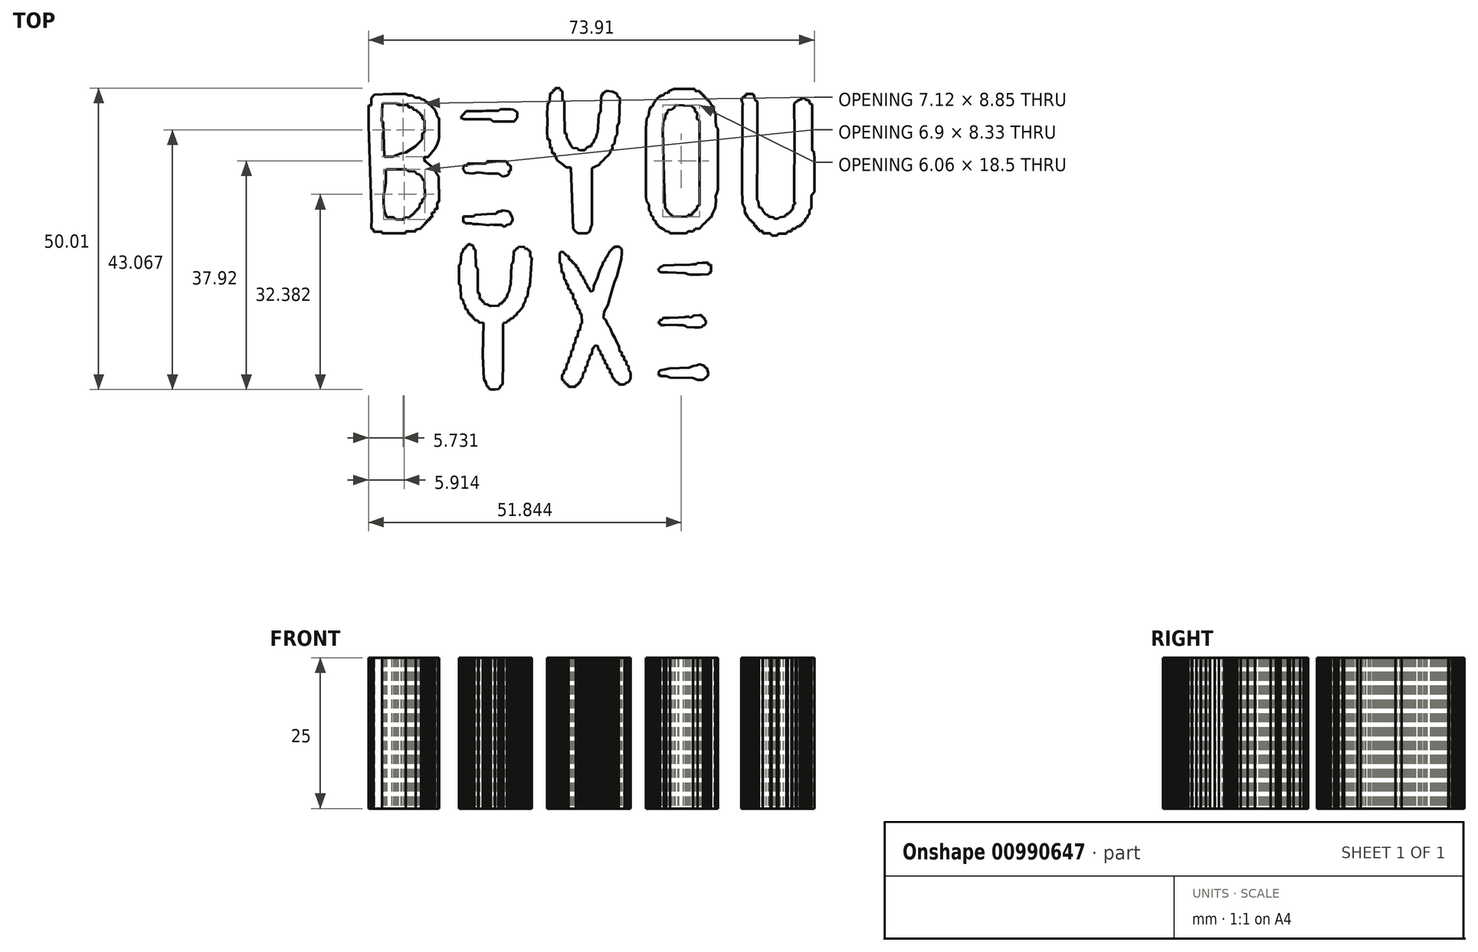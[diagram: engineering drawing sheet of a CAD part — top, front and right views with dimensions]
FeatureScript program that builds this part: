
annotation { "Feature Type Name" : "Feature", "Feature Type Description" : "" }
export const myFeature = defineFeature(function(context is Context, id is Id, definition is map)
    precondition{}
    {
        {
            var Q0;
            Q0=qCreatedBy(makeId("Top.planeOp"), FACE);
            var sketch = newSketch(context, id + "F0", { "sketchPlane" : qUnion([Q0])});
            skLineSegment(sketch, "E0", {"start": v(-34.3, -5.43) * mm, "end": v(-34.81, 9.8) * mm});
            skLineSegment(sketch, "E1", {"start": v(-34.81, 9.8) * mm, "end": v(-34.81, 13.18) * mm});
            skLineSegment(sketch, "E2", {"start": v(-34.81, 13.18) * mm, "end": v(-34.36, 13.18) * mm});
            skLineSegment(sketch, "E3", {"start": v(-34.36, 13.18) * mm, "end": v(-34.36, 14.36) * mm});
            skLineSegment(sketch, "E4", {"start": v(-34.36, 14.36) * mm, "end": v(-33.86, 14.98) * mm});
            skLineSegment(sketch, "E5", {"start": v(-33.86, 14.98) * mm, "end": v(-31, 15.08) * mm});
            skLineSegment(sketch, "E6", {"start": v(-31, 15.08) * mm, "end": v(-30.33, 15.08) * mm});
            skLineSegment(sketch, "E7", {"start": v(-30.33, 15.08) * mm, "end": v(-29.68, 15.08) * mm});
            skLineSegment(sketch, "E8", {"start": v(-29.68, 15.08) * mm, "end": v(-28.68, 15.08) * mm});
            skLineSegment(sketch, "E9", {"start": v(-28.68, 15.08) * mm, "end": v(-28.46, 14.98) * mm});
            skLineSegment(sketch, "E10", {"start": v(-28.46, 14.98) * mm, "end": v(-28.18, 14.86) * mm});
            skLineSegment(sketch, "E11", {"start": v(-28.18, 14.86) * mm, "end": v(-27.9, 14.86) * mm});
            skLineSegment(sketch, "E12", {"start": v(-27.9, 14.86) * mm, "end": v(-27.49, 14.86) * mm});
            skLineSegment(sketch, "E13", {"start": v(-27.49, 14.86) * mm, "end": v(-27.28, 14.62) * mm});
            skLineSegment(sketch, "E14", {"start": v(-27.28, 14.62) * mm, "end": v(-27.05, 14.47) * mm});
            skLineSegment(sketch, "E15", {"start": v(-27.05, 14.47) * mm, "end": v(-26.25, 14.47) * mm});
            skLineSegment(sketch, "E16", {"start": v(-26.25, 14.47) * mm, "end": v(-26.04, 14.22) * mm});
            skLineSegment(sketch, "E17", {"start": v(-26.04, 14.22) * mm, "end": v(-25.7, 14.11) * mm});
            skLineSegment(sketch, "E18", {"start": v(-25.7, 14.11) * mm, "end": v(-25.38, 14) * mm});
            skLineSegment(sketch, "E19", {"start": v(-25.38, 14) * mm, "end": v(-25.38, 13.8) * mm});
            skLineSegment(sketch, "E20", {"start": v(-25.38, 13.8) * mm, "end": v(-24.94, 13.68) * mm});
            skLineSegment(sketch, "E21", {"start": v(-24.94, 13.68) * mm, "end": v(-24.94, 13.52) * mm});
            skLineSegment(sketch, "E22", {"start": v(-24.94, 13.52) * mm, "end": v(-24.86, 13.42) * mm});
            skLineSegment(sketch, "E23", {"start": v(-24.86, 13.42) * mm, "end": v(-24.67, 13.33) * mm});
            skLineSegment(sketch, "E24", {"start": v(-24.67, 13.33) * mm, "end": v(-24.4, 13.23) * mm});
            skLineSegment(sketch, "E25", {"start": v(-24.4, 13.23) * mm, "end": v(-24.3, 12.92) * mm});
            skLineSegment(sketch, "E26", {"start": v(-24.3, 12.92) * mm, "end": v(-24.1, 12.8) * mm});
            skLineSegment(sketch, "E27", {"start": v(-24.1, 12.8) * mm, "end": v(-23.97, 12.65) * mm});
            skLineSegment(sketch, "E28", {"start": v(-23.97, 12.65) * mm, "end": v(-23.87, 12.54) * mm});
            skLineSegment(sketch, "E29", {"start": v(-23.87, 12.54) * mm, "end": v(-23.67, 12.15) * mm});
            skLineSegment(sketch, "E30", {"start": v(-23.67, 12.15) * mm, "end": v(-23.47, 11.72) * mm});
            skLineSegment(sketch, "E31", {"start": v(-23.47, 11.72) * mm, "end": v(-23.48, 11.48) * mm});
            skLineSegment(sketch, "E32", {"start": v(-23.48, 11.48) * mm, "end": v(-23.32, 11.22) * mm});
            skLineSegment(sketch, "E33", {"start": v(-23.32, 11.22) * mm, "end": v(-23.2, 11.12) * mm});
            skLineSegment(sketch, "E34", {"start": v(-23.2, 11.12) * mm, "end": v(-23.12, 10.84) * mm});
            skLineSegment(sketch, "E35", {"start": v(-23.12, 10.84) * mm, "end": v(-23.12, 7.9) * mm});
            skLineSegment(sketch, "E36", {"start": v(-23.12, 7.9) * mm, "end": v(-23.2, 7.48) * mm});
            skLineSegment(sketch, "E37", {"start": v(-23.2, 7.48) * mm, "end": v(-23.46, 6.68) * mm});
            skLineSegment(sketch, "E38", {"start": v(-23.46, 6.68) * mm, "end": v(-23.84, 5.97) * mm});
            skLineSegment(sketch, "E39", {"start": v(-23.84, 5.97) * mm, "end": v(-24.26, 5.45) * mm});
            skLineSegment(sketch, "E40", {"start": v(-24.26, 5.45) * mm, "end": v(-24.54, 5.11) * mm});
            skLineSegment(sketch, "E41", {"start": v(-24.54, 5.11) * mm, "end": v(-24.94, 4.62) * mm});
            skLineSegment(sketch, "E42", {"start": v(-24.94, 4.62) * mm, "end": v(-25.58, 4.62) * mm});
            skLineSegment(sketch, "E43", {"start": v(-25.58, 4.62) * mm, "end": v(-25.58, 4.23) * mm});
            skLineSegment(sketch, "E44", {"start": v(-25.58, 4.23) * mm, "end": v(-25.38, 3.9) * mm});
            skLineSegment(sketch, "E45", {"start": v(-25.38, 3.9) * mm, "end": v(-24.94, 3.54) * mm});
            skLineSegment(sketch, "E46", {"start": v(-24.94, 3.54) * mm, "end": v(-24.55, 3.21) * mm});
            skLineSegment(sketch, "E47", {"start": v(-24.55, 3.21) * mm, "end": v(-24.02, 2.79) * mm});
            skLineSegment(sketch, "E48", {"start": v(-24.02, 2.79) * mm, "end": v(-23.66, 2.15) * mm});
            skLineSegment(sketch, "E49", {"start": v(-23.66, 2.15) * mm, "end": v(-23.2, 1.35) * mm});
            skLineSegment(sketch, "E50", {"start": v(-23.2, 1.35) * mm, "end": v(-23.12, -2.78) * mm});
            skLineSegment(sketch, "E51", {"start": v(-23.12, -2.78) * mm, "end": v(-23.46, -2.97) * mm});
            skLineSegment(sketch, "E52", {"start": v(-23.46, -2.97) * mm, "end": v(-23.44, -3.7) * mm});
            skLineSegment(sketch, "E53", {"start": v(-23.44, -3.7) * mm, "end": v(-23.29, -3.98) * mm});
            skLineSegment(sketch, "E54", {"start": v(-23.29, -3.98) * mm, "end": v(-23.81, -3.98) * mm});
            skLineSegment(sketch, "E55", {"start": v(-23.81, -3.98) * mm, "end": v(-23.88, -4.63) * mm});
            skLineSegment(sketch, "E56", {"start": v(-23.88, -4.63) * mm, "end": v(-24.29, -4.64) * mm});
            skLineSegment(sketch, "E57", {"start": v(-24.29, -4.64) * mm, "end": v(-24.28, -5.37) * mm});
            skLineSegment(sketch, "E58", {"start": v(-24.28, -5.37) * mm, "end": v(-24.64, -5.37) * mm});
            skLineSegment(sketch, "E59", {"start": v(-24.64, -5.37) * mm, "end": v(-24.64, -5.8) * mm});
            skLineSegment(sketch, "E60", {"start": v(-24.64, -5.8) * mm, "end": v(-25.06, -5.8) * mm});
            skLineSegment(sketch, "E61", {"start": v(-25.06, -5.8) * mm, "end": v(-25.06, -6.16) * mm});
            skLineSegment(sketch, "E62", {"start": v(-25.06, -6.16) * mm, "end": v(-25.38, -6.16) * mm});
            skLineSegment(sketch, "E63", {"start": v(-25.38, -6.16) * mm, "end": v(-25.37, -6.52) * mm});
            skLineSegment(sketch, "E64", {"start": v(-25.37, -6.52) * mm, "end": v(-25.62, -6.67) * mm});
            skLineSegment(sketch, "E65", {"start": v(-25.62, -6.67) * mm, "end": v(-25.8, -6.9) * mm});
            skLineSegment(sketch, "E66", {"start": v(-25.8, -6.9) * mm, "end": v(-26.12, -7.07) * mm});
            skLineSegment(sketch, "E67", {"start": v(-26.12, -7.07) * mm, "end": v(-26.12, -7.3) * mm});
            skLineSegment(sketch, "E68", {"start": v(-26.12, -7.3) * mm, "end": v(-26.98, -7.38) * mm});
            skLineSegment(sketch, "E69", {"start": v(-26.98, -7.38) * mm, "end": v(-26.95, -7.7) * mm});
            skLineSegment(sketch, "E70", {"start": v(-26.95, -7.7) * mm, "end": v(-28.6, -7.7) * mm});
            skLineSegment(sketch, "E71", {"start": v(-28.6, -7.7) * mm, "end": v(-28.64, -8.06) * mm});
            skLineSegment(sketch, "E72", {"start": v(-28.64, -8.06) * mm, "end": v(-32.55, -8.06) * mm});
            skLineSegment(sketch, "E73", {"start": v(-32.55, -8.06) * mm, "end": v(-32.56, -7.78) * mm});
            skLineSegment(sketch, "E74", {"start": v(-32.56, -7.78) * mm, "end": v(-33.96, -7.78) * mm});
            skLineSegment(sketch, "E75", {"start": v(-33.96, -7.78) * mm, "end": v(-33.97, -7.37) * mm});
            skLineSegment(sketch, "E76", {"start": v(-33.97, -7.37) * mm, "end": v(-34.36, -7.3) * mm});
            skLineSegment(sketch, "E77", {"start": v(-34.36, -7.3) * mm, "end": v(-34.3, -5.43) * mm});
            skLineSegment(sketch, "E78", {"start": v(-19.52, 11.12) * mm, "end": v(-19.02, 11.74) * mm});
            skLineSegment(sketch, "E79", {"start": v(-19.02, 11.74) * mm, "end": v(-18.6, 12.25) * mm});
            skLineSegment(sketch, "E80", {"start": v(-18.6, 12.25) * mm, "end": v(-17.58, 12.25) * mm});
            skLineSegment(sketch, "E81", {"start": v(-17.58, 12.25) * mm, "end": v(-15.95, 12.25) * mm});
            skLineSegment(sketch, "E82", {"start": v(-15.95, 12.25) * mm, "end": v(-15.27, 12.26) * mm});
            skLineSegment(sketch, "E83", {"start": v(-15.27, 12.26) * mm, "end": v(-13.29, 12.3) * mm});
            skLineSegment(sketch, "E84", {"start": v(-13.29, 12.3) * mm, "end": v(-12.97, 12.54) * mm});
            skLineSegment(sketch, "E85", {"start": v(-12.97, 12.54) * mm, "end": v(-12.51, 12.54) * mm});
            skLineSegment(sketch, "E86", {"start": v(-12.51, 12.54) * mm, "end": v(-12.05, 12.54) * mm});
            skLineSegment(sketch, "E87", {"start": v(-12.05, 12.54) * mm, "end": v(-11.24, 12.54) * mm});
            skLineSegment(sketch, "E88", {"start": v(-11.24, 12.54) * mm, "end": v(-10.76, 12.5) * mm});
            skLineSegment(sketch, "E89", {"start": v(-10.76, 12.5) * mm, "end": v(-10.18, 12.02) * mm});
            skLineSegment(sketch, "E90", {"start": v(-10.18, 12.02) * mm, "end": v(-10.16, 11.12) * mm});
            skLineSegment(sketch, "E91", {"start": v(-10.16, 11.12) * mm, "end": v(-10.66, 10.52) * mm});
            skLineSegment(sketch, "E92", {"start": v(-10.66, 10.52) * mm, "end": v(-11.52, 10.52) * mm});
            skLineSegment(sketch, "E93", {"start": v(-11.52, 10.52) * mm, "end": v(-14.14, 10.52) * mm});
            skLineSegment(sketch, "E94", {"start": v(-14.14, 10.52) * mm, "end": v(-14.57, 10.87) * mm});
            skLineSegment(sketch, "E95", {"start": v(-14.57, 10.87) * mm, "end": v(-15.38, 10.87) * mm});
            skLineSegment(sketch, "E96", {"start": v(-15.38, 10.87) * mm, "end": v(-18.96, 10.87) * mm});
            skLineSegment(sketch, "E97", {"start": v(-18.96, 10.87) * mm, "end": v(-19.52, 11.12) * mm});
            skLineSegment(sketch, "E98", {"start": v(-19.13, 2.59) * mm, "end": v(-19.08, 3.18) * mm});
            skLineSegment(sketch, "E99", {"start": v(-19.08, 3.18) * mm, "end": v(-18.7, 3.18) * mm});
            skLineSegment(sketch, "E100", {"start": v(-18.7, 3.18) * mm, "end": v(-18.43, 3.18) * mm});
            skLineSegment(sketch, "E101", {"start": v(-18.43, 3.18) * mm, "end": v(-18.43, 3.54) * mm});
            skLineSegment(sketch, "E102", {"start": v(-18.43, 3.54) * mm, "end": v(-16.83, 3.54) * mm});
            skLineSegment(sketch, "E103", {"start": v(-16.83, 3.54) * mm, "end": v(-15.38, 3.54) * mm});
            skLineSegment(sketch, "E104", {"start": v(-15.38, 3.54) * mm, "end": v(-15.01, 4) * mm});
            skLineSegment(sketch, "E105", {"start": v(-15.01, 4) * mm, "end": v(-14.15, 3.9) * mm});
            skLineSegment(sketch, "E106", {"start": v(-14.15, 3.9) * mm, "end": v(-13.26, 3.9) * mm});
            skLineSegment(sketch, "E107", {"start": v(-13.26, 3.9) * mm, "end": v(-12.37, 3.9) * mm});
            skLineSegment(sketch, "E108", {"start": v(-12.37, 3.9) * mm, "end": v(-11.95, 3.9) * mm});
            skLineSegment(sketch, "E109", {"start": v(-11.95, 3.9) * mm, "end": v(-11.53, 3.18) * mm});
            skLineSegment(sketch, "E110", {"start": v(-11.53, 3.18) * mm, "end": v(-11.24, 3.18) * mm});
            skLineSegment(sketch, "E111", {"start": v(-11.24, 3.18) * mm, "end": v(-11.22, 2.3) * mm});
            skLineSegment(sketch, "E112", {"start": v(-11.22, 2.3) * mm, "end": v(-11.52, 2.3) * mm});
            skLineSegment(sketch, "E113", {"start": v(-11.52, 2.3) * mm, "end": v(-11.51, 1.88) * mm});
            skLineSegment(sketch, "E114", {"start": v(-11.51, 1.88) * mm, "end": v(-11.8, 1.53) * mm});
            skLineSegment(sketch, "E115", {"start": v(-11.8, 1.53) * mm, "end": v(-12.58, 1.35) * mm});
            skLineSegment(sketch, "E116", {"start": v(-12.58, 1.35) * mm, "end": v(-13.23, 1.88) * mm});
            skLineSegment(sketch, "E117", {"start": v(-13.23, 1.88) * mm, "end": v(-14.57, 1.88) * mm});
            skLineSegment(sketch, "E118", {"start": v(-14.57, 1.88) * mm, "end": v(-15.1, 1.88) * mm});
            skLineSegment(sketch, "E119", {"start": v(-15.1, 1.88) * mm, "end": v(-15.83, 1.96) * mm});
            skLineSegment(sketch, "E120", {"start": v(-15.83, 1.96) * mm, "end": v(-16.64, 2.04) * mm});
            skLineSegment(sketch, "E121", {"start": v(-16.64, 2.04) * mm, "end": v(-17.58, 1.88) * mm});
            skLineSegment(sketch, "E122", {"start": v(-17.58, 1.88) * mm, "end": v(-18.7, 2) * mm});
            skLineSegment(sketch, "E123", {"start": v(-18.7, 2) * mm, "end": v(-19.13, 2.59) * mm});
            skLineSegment(sketch, "E124", {"start": v(-18.8, -6.4) * mm, "end": v(-18.8, -6.17) * mm});
            skLineSegment(sketch, "E125", {"start": v(-18.8, -6.17) * mm, "end": v(-19.13, -6.17) * mm});
            skLineSegment(sketch, "E126", {"start": v(-19.13, -6.17) * mm, "end": v(-19.14, -5.83) * mm});
            skLineSegment(sketch, "E127", {"start": v(-19.14, -5.83) * mm, "end": v(-19.13, -5.77) * mm});
            skLineSegment(sketch, "E128", {"start": v(-19.13, -5.77) * mm, "end": v(-19.14, -5.64) * mm});
            skLineSegment(sketch, "E129", {"start": v(-19.14, -5.64) * mm, "end": v(-19.1, -5.27) * mm});
            skLineSegment(sketch, "E130", {"start": v(-19.1, -5.27) * mm, "end": v(-18.4, -5.27) * mm});
            skLineSegment(sketch, "E131", {"start": v(-18.4, -5.27) * mm, "end": v(-17.37, -5.27) * mm});
            skLineSegment(sketch, "E132", {"start": v(-17.37, -5.27) * mm, "end": v(-17.13, -4.97) * mm});
            skLineSegment(sketch, "E133", {"start": v(-17.13, -4.97) * mm, "end": v(-14.14, -4.8) * mm});
            skLineSegment(sketch, "E134", {"start": v(-14.14, -4.8) * mm, "end": v(-13.74, -4.85) * mm});
            skLineSegment(sketch, "E135", {"start": v(-13.74, -4.85) * mm, "end": v(-13.53, -4.6) * mm});
            skLineSegment(sketch, "E136", {"start": v(-13.53, -4.6) * mm, "end": v(-13.19, -4.4) * mm});
            skLineSegment(sketch, "E137", {"start": v(-13.19, -4.4) * mm, "end": v(-12.9, -4.4) * mm});
            skLineSegment(sketch, "E138", {"start": v(-12.9, -4.4) * mm, "end": v(-12.58, -4.22) * mm});
            skLineSegment(sketch, "E139", {"start": v(-12.58, -4.22) * mm, "end": v(-11.84, -4.35) * mm});
            skLineSegment(sketch, "E140", {"start": v(-11.84, -4.35) * mm, "end": v(-11.51, -4.45) * mm});
            skLineSegment(sketch, "E141", {"start": v(-11.51, -4.45) * mm, "end": v(-10.98, -5.38) * mm});
            skLineSegment(sketch, "E142", {"start": v(-10.98, -5.38) * mm, "end": v(-10.9, -5.78) * mm});
            skLineSegment(sketch, "E143", {"start": v(-10.9, -5.78) * mm, "end": v(-11.05, -6.12) * mm});
            skLineSegment(sketch, "E144", {"start": v(-11.05, -6.12) * mm, "end": v(-11.3, -6.5) * mm});
            skLineSegment(sketch, "E145", {"start": v(-11.3, -6.5) * mm, "end": v(-11.9, -6.63) * mm});
            skLineSegment(sketch, "E146", {"start": v(-11.9, -6.63) * mm, "end": v(-12.11, -6.9) * mm});
            skLineSegment(sketch, "E147", {"start": v(-12.11, -6.9) * mm, "end": v(-12.58, -6.9) * mm});
            skLineSegment(sketch, "E148", {"start": v(-12.58, -6.9) * mm, "end": v(-12.65, -6.63) * mm});
            skLineSegment(sketch, "E149", {"start": v(-12.65, -6.63) * mm, "end": v(-14.07, -6.63) * mm});
            skLineSegment(sketch, "E150", {"start": v(-14.07, -6.63) * mm, "end": v(-14.57, -6.58) * mm});
            skLineSegment(sketch, "E151", {"start": v(-14.57, -6.58) * mm, "end": v(-14.78, -6.7) * mm});
            skLineSegment(sketch, "E152", {"start": v(-14.78, -6.7) * mm, "end": v(-15.54, -6.63) * mm});
            skLineSegment(sketch, "E153", {"start": v(-15.54, -6.63) * mm, "end": v(-15.87, -6.6) * mm});
            skLineSegment(sketch, "E154", {"start": v(-15.87, -6.6) * mm, "end": v(-16.53, -6.53) * mm});
            skLineSegment(sketch, "E155", {"start": v(-16.53, -6.53) * mm, "end": v(-17.17, -6.53) * mm});
            skLineSegment(sketch, "E156", {"start": v(-17.17, -6.53) * mm, "end": v(-17.48, -6.5) * mm});
            skLineSegment(sketch, "E157", {"start": v(-17.48, -6.5) * mm, "end": v(-17.78, -6.38) * mm});
            skLineSegment(sketch, "E158", {"start": v(-17.78, -6.38) * mm, "end": v(-18.1, -6.38) * mm});
            skLineSegment(sketch, "E159", {"start": v(-18.1, -6.38) * mm, "end": v(-18.8, -6.4) * mm});
            skLineSegment(sketch, "E160", {"start": v(-3.75, 16.06) * mm, "end": v(-3.92, 15.96) * mm});
            skLineSegment(sketch, "E161", {"start": v(-3.92, 15.96) * mm, "end": v(-3.9, 15.67) * mm});
            skLineSegment(sketch, "E162", {"start": v(-3.9, 15.67) * mm, "end": v(-4.2, 15.67) * mm});
            skLineSegment(sketch, "E163", {"start": v(-4.2, 15.67) * mm, "end": v(-4.3, 15.56) * mm});
            skLineSegment(sketch, "E164", {"start": v(-4.3, 15.56) * mm, "end": v(-4.28, 15.3) * mm});
            skLineSegment(sketch, "E165", {"start": v(-4.28, 15.3) * mm, "end": v(-4.47, 15.2) * mm});
            skLineSegment(sketch, "E166", {"start": v(-4.47, 15.2) * mm, "end": v(-4.68, 15.2) * mm});
            skLineSegment(sketch, "E167", {"start": v(-4.68, 15.2) * mm, "end": v(-4.66, 14.98) * mm});
            skLineSegment(sketch, "E168", {"start": v(-4.66, 14.98) * mm, "end": v(-4.8, 13.6) * mm});
            skLineSegment(sketch, "E169", {"start": v(-4.8, 13.6) * mm, "end": v(-5.05, 13.6) * mm});
            skLineSegment(sketch, "E170", {"start": v(-5.05, 13.6) * mm, "end": v(-5.22, 11.93) * mm});
            skLineSegment(sketch, "E171", {"start": v(-5.22, 11.93) * mm, "end": v(-5.13, 10.54) * mm});
            skPoint(sketch, "E171.endSnap0", {"position": v(-5.13, 12.76) * mm});
            skLineSegment(sketch, "E172", {"start": v(-5.13, 10.54) * mm, "end": v(-5.22, 8.93) * mm});
            skLineSegment(sketch, "E173", {"start": v(-5.22, 8.93) * mm, "end": v(-5.13, 7.52) * mm});
            skLineSegment(sketch, "E174", {"start": v(-5.13, 7.52) * mm, "end": v(-4.79, 7.52) * mm});
            skLineSegment(sketch, "E175", {"start": v(-4.79, 7.52) * mm, "end": v(-4.68, 6.1) * mm});
            skLineSegment(sketch, "E176", {"start": v(-4.68, 6.1) * mm, "end": v(-4.44, 6.23) * mm});
            skLineSegment(sketch, "E177", {"start": v(-4.44, 6.23) * mm, "end": v(-4.38, 5.25) * mm});
            skLineSegment(sketch, "E178", {"start": v(-4.38, 5.25) * mm, "end": v(-3.96, 5.25) * mm});
            skLineSegment(sketch, "E179", {"start": v(-3.96, 5.25) * mm, "end": v(-3.92, 4.62) * mm});
            skLineSegment(sketch, "E180", {"start": v(-3.92, 4.62) * mm, "end": v(-3.56, 4.62) * mm});
            skLineSegment(sketch, "E181", {"start": v(-3.56, 4.62) * mm, "end": v(-3.72, 4.42) * mm});
            skLineSegment(sketch, "E182", {"start": v(-3.72, 4.42) * mm, "end": v(-3.49, 4) * mm});
            skLineSegment(sketch, "E183", {"start": v(-3.49, 4) * mm, "end": v(-2.52, 3.34) * mm});
            skLineSegment(sketch, "E184", {"start": v(-2.52, 3.34) * mm, "end": v(-2, 2.91) * mm});
            skLineSegment(sketch, "E185", {"start": v(-2, 2.91) * mm, "end": v(-1.24, 2.91) * mm});
            skLineSegment(sketch, "E186", {"start": v(-1.24, 2.91) * mm, "end": v(-0.86, -7.3) * mm});
            skLineSegment(sketch, "E187", {"start": v(-0.86, -7.3) * mm, "end": v(-0.47, -7.7) * mm});
            skLineSegment(sketch, "E188", {"start": v(-0.47, -7.7) * mm, "end": v(-0.13, -8.06) * mm});
            skLineSegment(sketch, "E189", {"start": v(-0.13, -8.06) * mm, "end": v(1.46, -8.06) * mm});
            skLineSegment(sketch, "E190", {"start": v(1.46, -8.06) * mm, "end": v(1.86, -7.7) * mm});
            skLineSegment(sketch, "E191", {"start": v(1.86, -7.7) * mm, "end": v(2.1, -6.9) * mm});
            skLineSegment(sketch, "E192", {"start": v(2.1, -6.9) * mm, "end": v(2.22, -6.66) * mm});
            skLineSegment(sketch, "E193", {"start": v(2.22, -6.66) * mm, "end": v(2.26, 2.78) * mm});
            skLineSegment(sketch, "E194", {"start": v(2.26, 2.78) * mm, "end": v(2.62, 2.98) * mm});
            skLineSegment(sketch, "E195", {"start": v(2.62, 2.98) * mm, "end": v(3.42, 3.35) * mm});
            skLineSegment(sketch, "E196", {"start": v(3.42, 3.35) * mm, "end": v(3.71, 3.7) * mm});
            skLineSegment(sketch, "E197", {"start": v(3.71, 3.7) * mm, "end": v(4.14, 4.12) * mm});
            skLineSegment(sketch, "E198", {"start": v(4.14, 4.12) * mm, "end": v(4.45, 4.5) * mm});
            skLineSegment(sketch, "E199", {"start": v(4.45, 4.5) * mm, "end": v(4.88, 4.85) * mm});
            skLineSegment(sketch, "E200", {"start": v(4.88, 4.85) * mm, "end": v(5.2, 5.25) * mm});
            skLineSegment(sketch, "E201", {"start": v(5.2, 5.25) * mm, "end": v(5.42, 5.87) * mm});
            skLineSegment(sketch, "E202", {"start": v(5.42, 5.87) * mm, "end": v(5.63, 5.87) * mm});
            skLineSegment(sketch, "E203", {"start": v(5.63, 5.87) * mm, "end": v(5.62, 6.54) * mm});
            skLineSegment(sketch, "E204", {"start": v(5.62, 6.54) * mm, "end": v(5.98, 6.85) * mm});
            skLineSegment(sketch, "E205", {"start": v(5.98, 6.85) * mm, "end": v(6.08, 7.9) * mm});
            skLineSegment(sketch, "E206", {"start": v(6.08, 7.9) * mm, "end": v(6.43, 8.34) * mm});
            skLineSegment(sketch, "E207", {"start": v(6.43, 8.34) * mm, "end": v(6.43, 9.7) * mm});
            skLineSegment(sketch, "E208", {"start": v(6.43, 9.7) * mm, "end": v(6.75, 10.38) * mm});
            skLineSegment(sketch, "E209", {"start": v(6.75, 10.38) * mm, "end": v(6.87, 14.36) * mm});
            skLineSegment(sketch, "E210", {"start": v(6.87, 14.36) * mm, "end": v(6.42, 14.73) * mm});
            skLineSegment(sketch, "E211", {"start": v(6.42, 14.73) * mm, "end": v(6.4, 15.1) * mm});
            skLineSegment(sketch, "E212", {"start": v(6.4, 15.1) * mm, "end": v(5.69, 15.5) * mm});
            skLineSegment(sketch, "E213", {"start": v(5.69, 15.5) * mm, "end": v(4.72, 15.59) * mm});
            skLineSegment(sketch, "E214", {"start": v(4.72, 15.59) * mm, "end": v(4.14, 15.25) * mm});
            skLineSegment(sketch, "E215", {"start": v(4.14, 15.25) * mm, "end": v(3.73, 14.65) * mm});
            skLineSegment(sketch, "E216", {"start": v(3.73, 14.65) * mm, "end": v(3.72, 12.2) * mm});
            skLineSegment(sketch, "E217", {"start": v(3.72, 12.2) * mm, "end": v(3.36, 11.56) * mm});
            skLineSegment(sketch, "E218", {"start": v(3.36, 11.56) * mm, "end": v(3.2, 8.68) * mm});
            skLineSegment(sketch, "E219", {"start": v(3.2, 8.68) * mm, "end": v(3.04, 8.49) * mm});
            skLineSegment(sketch, "E220", {"start": v(3.04, 8.49) * mm, "end": v(2.89, 7.69) * mm});
            skLineSegment(sketch, "E221", {"start": v(2.89, 7.69) * mm, "end": v(2.65, 7.57) * mm});
            skLineSegment(sketch, "E222", {"start": v(2.65, 7.57) * mm, "end": v(2.46, 7) * mm});
            skLineSegment(sketch, "E223", {"start": v(2.46, 7) * mm, "end": v(2.24, 6.84) * mm});
            skLineSegment(sketch, "E224", {"start": v(2.24, 6.84) * mm, "end": v(2.1, 6.4) * mm});
            skLineSegment(sketch, "E225", {"start": v(2.1, 6.4) * mm, "end": v(1.79, 6.4) * mm});
            skLineSegment(sketch, "E226", {"start": v(1.79, 6.4) * mm, "end": v(1.25, 6.1) * mm});
            skLineSegment(sketch, "E227", {"start": v(1.25, 6.1) * mm, "end": v(1.06, 5.76) * mm});
            skLineSegment(sketch, "E228", {"start": v(1.06, 5.76) * mm, "end": v(0.62, 5.78) * mm});
            skLineSegment(sketch, "E229", {"start": v(0.62, 5.78) * mm, "end": v(0.31, 5.78) * mm});
            skLineSegment(sketch, "E230", {"start": v(0.31, 5.78) * mm, "end": v(0, 5.82) * mm});
            skLineSegment(sketch, "E231", {"start": v(0, 5.82) * mm, "end": v(-0.2, 6.04) * mm});
            skLineSegment(sketch, "E232", {"start": v(-0.2, 6.04) * mm, "end": v(-0.96, 6.12) * mm});
            skLineSegment(sketch, "E233", {"start": v(-0.96, 6.12) * mm, "end": v(-1.24, 6.5) * mm});
            skLineSegment(sketch, "E234", {"start": v(-1.24, 6.5) * mm, "end": v(-1.61, 7.24) * mm});
            skLineSegment(sketch, "E235", {"start": v(-1.61, 7.24) * mm, "end": v(-1.96, 7.77) * mm});
            skLineSegment(sketch, "E236", {"start": v(-1.96, 7.77) * mm, "end": v(-1.93, 8.47) * mm});
            skLineSegment(sketch, "E237", {"start": v(-1.93, 8.47) * mm, "end": v(-2.28, 8.5) * mm});
            skLineSegment(sketch, "E238", {"start": v(-2.28, 8.5) * mm, "end": v(-2.36, 12.53) * mm});
            skLineSegment(sketch, "E239", {"start": v(-2.36, 12.53) * mm, "end": v(-2.36, 13.87) * mm});
            skLineSegment(sketch, "E240", {"start": v(-2.36, 13.87) * mm, "end": v(-2.64, 14) * mm});
            skLineSegment(sketch, "E241", {"start": v(-2.64, 14) * mm, "end": v(-2.66, 15.52) * mm});
            skLineSegment(sketch, "E242", {"start": v(-2.66, 15.52) * mm, "end": v(-3.11, 15.77) * mm});
            skLineSegment(sketch, "E243", {"start": v(-3.11, 15.77) * mm, "end": v(-3.07, 16.04) * mm});
            skLineSegment(sketch, "E244", {"start": v(-3.07, 16.04) * mm, "end": v(-3.75, 16.06) * mm});
            skLineSegment(sketch, "E245", {"start": v(15.83, 15.93) * mm, "end": v(15.04, 15.57) * mm});
            skLineSegment(sketch, "E246", {"start": v(15.04, 15.57) * mm, "end": v(14.87, 15.28) * mm});
            skLineSegment(sketch, "E247", {"start": v(14.87, 15.28) * mm, "end": v(14.32, 15.2) * mm});
            skLineSegment(sketch, "E248", {"start": v(14.32, 15.2) * mm, "end": v(14.04, 14.81) * mm});
            skLineSegment(sketch, "E249", {"start": v(14.04, 14.81) * mm, "end": v(13.6, 14.81) * mm});
            skLineSegment(sketch, "E250", {"start": v(13.6, 14.81) * mm, "end": v(13.41, 14.48) * mm});
            skLineSegment(sketch, "E251", {"start": v(13.41, 14.48) * mm, "end": v(13.2, 14.48) * mm});
            skLineSegment(sketch, "E252", {"start": v(13.2, 14.48) * mm, "end": v(12.8, 14) * mm});
            skLineSegment(sketch, "E253", {"start": v(12.8, 14) * mm, "end": v(12.5, 13.63) * mm});
            skLineSegment(sketch, "E254", {"start": v(12.5, 13.63) * mm, "end": v(12.25, 13) * mm});
            skLineSegment(sketch, "E255", {"start": v(12.25, 13) * mm, "end": v(12.05, 13.01) * mm});
            skLineSegment(sketch, "E256", {"start": v(12.05, 13.01) * mm, "end": v(11.73, 12.45) * mm});
            skLineSegment(sketch, "E257", {"start": v(11.73, 12.45) * mm, "end": v(11.63, 11.4) * mm});
            skLineSegment(sketch, "E258", {"start": v(11.63, 11.4) * mm, "end": v(11.32, 11.03) * mm});
            skLineSegment(sketch, "E259", {"start": v(11.32, 11.03) * mm, "end": v(11.15, 9.34) * mm});
            skLineSegment(sketch, "E260", {"start": v(11.15, 9.34) * mm, "end": v(11.15, -2.03) * mm});
            skLineSegment(sketch, "E261", {"start": v(11.15, -2.03) * mm, "end": v(11.32, -2.78) * mm});
            skLineSegment(sketch, "E262", {"start": v(11.32, -2.78) * mm, "end": v(11.68, -3.27) * mm});
            skLineSegment(sketch, "E263", {"start": v(11.68, -3.27) * mm, "end": v(11.68, -4.24) * mm});
            skLineSegment(sketch, "E264", {"start": v(11.68, -4.24) * mm, "end": v(12.03, -4.64) * mm});
            skLineSegment(sketch, "E265", {"start": v(12.03, -4.64) * mm, "end": v(12.04, -5.02) * mm});
            skLineSegment(sketch, "E266", {"start": v(12.04, -5.02) * mm, "end": v(12.4, -5.33) * mm});
            skLineSegment(sketch, "E267", {"start": v(12.4, -5.33) * mm, "end": v(12.42, -5.77) * mm});
            skLineSegment(sketch, "E268", {"start": v(12.42, -5.77) * mm, "end": v(12.82, -6.1) * mm});
            skLineSegment(sketch, "E269", {"start": v(12.82, -6.1) * mm, "end": v(12.8, -6.43) * mm});
            skLineSegment(sketch, "E270", {"start": v(12.8, -6.43) * mm, "end": v(13.23, -6.66) * mm});
            skLineSegment(sketch, "E271", {"start": v(13.23, -6.66) * mm, "end": v(13.21, -6.88) * mm});
            skLineSegment(sketch, "E272", {"start": v(13.21, -6.88) * mm, "end": v(13.6, -7.06) * mm});
            skLineSegment(sketch, "E273", {"start": v(13.6, -7.06) * mm, "end": v(13.89, -7.3) * mm});
            skLineSegment(sketch, "E274", {"start": v(13.89, -7.3) * mm, "end": v(14.28, -7.44) * mm});
            skLineSegment(sketch, "E275", {"start": v(14.28, -7.44) * mm, "end": v(14.32, -7.64) * mm});
            skLineSegment(sketch, "E276", {"start": v(14.32, -7.64) * mm, "end": v(15.08, -7.81) * mm});
            skLineSegment(sketch, "E277", {"start": v(15.08, -7.81) * mm, "end": v(15.1, -8.06) * mm});
            skLineSegment(sketch, "E278", {"start": v(15.1, -8.06) * mm, "end": v(17.93, -8.06) * mm});
            skLineSegment(sketch, "E279", {"start": v(17.93, -8.06) * mm, "end": v(18.14, -7.7) * mm});
            skLineSegment(sketch, "E280", {"start": v(18.14, -7.7) * mm, "end": v(19.08, -7.7) * mm});
            skLineSegment(sketch, "E281", {"start": v(19.08, -7.7) * mm, "end": v(19.33, -7.26) * mm});
            skLineSegment(sketch, "E282", {"start": v(19.33, -7.26) * mm, "end": v(20.07, -7.3) * mm});
            skLineSegment(sketch, "E283", {"start": v(20.07, -7.3) * mm, "end": v(20.42, -6.87) * mm});
            skLineSegment(sketch, "E284", {"start": v(20.42, -6.87) * mm, "end": v(20.65, -6.55) * mm});
            skLineSegment(sketch, "E285", {"start": v(20.65, -6.55) * mm, "end": v(20.92, -6.4) * mm});
            skLineSegment(sketch, "E286", {"start": v(20.92, -6.4) * mm, "end": v(21.21, -6.1) * mm});
            skLineSegment(sketch, "E287", {"start": v(21.21, -6.1) * mm, "end": v(21.35, -5.84) * mm});
            skLineSegment(sketch, "E288", {"start": v(21.35, -5.84) * mm, "end": v(21.55, -5.82) * mm});
            skLineSegment(sketch, "E289", {"start": v(21.55, -5.82) * mm, "end": v(21.77, -5.43) * mm});
            skLineSegment(sketch, "E290", {"start": v(21.77, -5.43) * mm, "end": v(21.96, -5.42) * mm});
            skLineSegment(sketch, "E291", {"start": v(21.96, -5.42) * mm, "end": v(22.32, -4.64) * mm});
            skLineSegment(sketch, "E292", {"start": v(22.32, -4.64) * mm, "end": v(22.7, -3.83) * mm});
            skLineSegment(sketch, "E293", {"start": v(22.7, -3.83) * mm, "end": v(22.8, -2.67) * mm});
            skLineSegment(sketch, "E294", {"start": v(22.8, -2.67) * mm, "end": v(22.76, -1.9) * mm});
            skLineSegment(sketch, "E295", {"start": v(22.76, -1.9) * mm, "end": v(23, -1.24) * mm});
            skLineSegment(sketch, "E296", {"start": v(23, -1.24) * mm, "end": v(23.1, -0.82) * mm});
            skLineSegment(sketch, "E297", {"start": v(23.1, -0.82) * mm, "end": v(23.12, 5.61) * mm});
            skLineSegment(sketch, "E298", {"start": v(23.12, 5.61) * mm, "end": v(23.12, 9.33) * mm});
            skLineSegment(sketch, "E299", {"start": v(23.12, 9.33) * mm, "end": v(22.81, 9.66) * mm});
            skLineSegment(sketch, "E300", {"start": v(22.81, 9.66) * mm, "end": v(22.73, 10.69) * mm});
            skLineSegment(sketch, "E301", {"start": v(22.73, 10.69) * mm, "end": v(22.7, 11.93) * mm});
            skLineSegment(sketch, "E302", {"start": v(22.7, 11.93) * mm, "end": v(22.4, 12.1) * mm});
            skLineSegment(sketch, "E303", {"start": v(22.4, 12.1) * mm, "end": v(22.4, 12.96) * mm});
            skLineSegment(sketch, "E304", {"start": v(22.4, 12.96) * mm, "end": v(21.94, 13.23) * mm});
            skLineSegment(sketch, "E305", {"start": v(21.94, 13.23) * mm, "end": v(21.91, 13.63) * mm});
            skLineSegment(sketch, "E306", {"start": v(21.91, 13.63) * mm, "end": v(21.66, 13.75) * mm});
            skLineSegment(sketch, "E307", {"start": v(21.66, 13.75) * mm, "end": v(21.6, 14.07) * mm});
            skLineSegment(sketch, "E308", {"start": v(21.6, 14.07) * mm, "end": v(21.28, 14.07) * mm});
            skLineSegment(sketch, "E309", {"start": v(21.28, 14.07) * mm, "end": v(21.23, 14.39) * mm});
            skLineSegment(sketch, "E310", {"start": v(21.23, 14.39) * mm, "end": v(20.8, 14.5) * mm});
            skLineSegment(sketch, "E311", {"start": v(20.8, 14.5) * mm, "end": v(20.86, 14.84) * mm});
            skLineSegment(sketch, "E312", {"start": v(20.86, 14.84) * mm, "end": v(20.5, 14.9) * mm});
            skLineSegment(sketch, "E313", {"start": v(20.5, 14.9) * mm, "end": v(20.48, 15.2) * mm});
            skLineSegment(sketch, "E314", {"start": v(20.48, 15.2) * mm, "end": v(20.11, 15.25) * mm});
            skLineSegment(sketch, "E315", {"start": v(20.11, 15.25) * mm, "end": v(20.07, 15.56) * mm});
            skLineSegment(sketch, "E316", {"start": v(20.07, 15.56) * mm, "end": v(19.55, 15.53) * mm});
            skLineSegment(sketch, "E317", {"start": v(19.55, 15.53) * mm, "end": v(19.33, 15.67) * mm});
            skLineSegment(sketch, "E318", {"start": v(19.33, 15.67) * mm, "end": v(19.3, 15.92) * mm});
            skLineSegment(sketch, "E319", {"start": v(19.3, 15.92) * mm, "end": v(18.52, 15.92) * mm});
            skLineSegment(sketch, "E320", {"start": v(18.52, 15.92) * mm, "end": v(15.83, 15.93) * mm});
            skLineSegment(sketch, "E321", {"start": v(29.1, 14.76) * mm, "end": v(28.95, 15.1) * mm});
            skLineSegment(sketch, "E322", {"start": v(28.95, 15.1) * mm, "end": v(27.76, 15.06) * mm});
            skLineSegment(sketch, "E323", {"start": v(27.76, 15.06) * mm, "end": v(27.77, 14.72) * mm});
            skLineSegment(sketch, "E324", {"start": v(27.77, 14.72) * mm, "end": v(27.36, 14.72) * mm});
            skLineSegment(sketch, "E325", {"start": v(27.36, 14.72) * mm, "end": v(27.27, 14.36) * mm});
            skLineSegment(sketch, "E326", {"start": v(27.27, 14.36) * mm, "end": v(27, 14.3) * mm});
            skLineSegment(sketch, "E327", {"start": v(27, 14.3) * mm, "end": v(27.05, 14) * mm});
            skLineSegment(sketch, "E328", {"start": v(27.05, 14) * mm, "end": v(27.1, 13.76) * mm});
            skLineSegment(sketch, "E329", {"start": v(27.1, 13.76) * mm, "end": v(27.23, 13.58) * mm});
            skLineSegment(sketch, "E330", {"start": v(27.23, 13.58) * mm, "end": v(27.2, 12.84) * mm});
            skLineSegment(sketch, "E331", {"start": v(27.2, 12.84) * mm, "end": v(27.14, -0.5) * mm});
            skLineSegment(sketch, "E332", {"start": v(27.14, -0.5) * mm, "end": v(27.2, -3.06) * mm});
            skLineSegment(sketch, "E333", {"start": v(27.2, -3.06) * mm, "end": v(27.56, -3.83) * mm});
            skLineSegment(sketch, "E334", {"start": v(27.56, -3.83) * mm, "end": v(27.6, -4.52) * mm});
            skLineSegment(sketch, "E335", {"start": v(27.6, -4.52) * mm, "end": v(27.99, -5.22) * mm});
            skLineSegment(sketch, "E336", {"start": v(27.99, -5.22) * mm, "end": v(28.36, -5.84) * mm});
            skLineSegment(sketch, "E337", {"start": v(28.36, -5.84) * mm, "end": v(28.7, -5.94) * mm});
            skLineSegment(sketch, "E338", {"start": v(28.7, -5.94) * mm, "end": v(28.69, -6.18) * mm});
            skLineSegment(sketch, "E339", {"start": v(28.69, -6.18) * mm, "end": v(29.06, -6.28) * mm});
            skLineSegment(sketch, "E340", {"start": v(29.06, -6.28) * mm, "end": v(29.13, -6.81) * mm});
            skLineSegment(sketch, "E341", {"start": v(29.13, -6.81) * mm, "end": v(29.52, -6.85) * mm});
            skLineSegment(sketch, "E342", {"start": v(29.52, -6.85) * mm, "end": v(29.53, -7.26) * mm});
            skLineSegment(sketch, "E343", {"start": v(29.53, -7.26) * mm, "end": v(29.91, -7.3) * mm});
            skLineSegment(sketch, "E344", {"start": v(29.91, -7.3) * mm, "end": v(29.9, -7.62) * mm});
            skLineSegment(sketch, "E345", {"start": v(29.9, -7.62) * mm, "end": v(30.54, -7.67) * mm});
            skLineSegment(sketch, "E346", {"start": v(30.54, -7.67) * mm, "end": v(30.57, -8.02) * mm});
            skLineSegment(sketch, "E347", {"start": v(30.57, -8.02) * mm, "end": v(31.84, -8.06) * mm});
            skLineSegment(sketch, "E348", {"start": v(31.84, -8.06) * mm, "end": v(32.03, -8.39) * mm});
            skLineSegment(sketch, "E349", {"start": v(32.03, -8.39) * mm, "end": v(32.93, -8.41) * mm});
            skLineSegment(sketch, "E350", {"start": v(32.93, -8.41) * mm, "end": v(33.13, -8.1) * mm});
            skLineSegment(sketch, "E351", {"start": v(33.13, -8.1) * mm, "end": v(34.47, -8.07) * mm});
            skLineSegment(sketch, "E352", {"start": v(34.47, -8.07) * mm, "end": v(34.68, -7.69) * mm});
            skLineSegment(sketch, "E353", {"start": v(34.68, -7.69) * mm, "end": v(35.29, -7.69) * mm});
            skLineSegment(sketch, "E354", {"start": v(35.29, -7.69) * mm, "end": v(35.47, -7.3) * mm});
            skLineSegment(sketch, "E355", {"start": v(35.47, -7.3) * mm, "end": v(36, -7.3) * mm});
            skLineSegment(sketch, "E356", {"start": v(36, -7.3) * mm, "end": v(36.2, -6.9) * mm});
            skLineSegment(sketch, "E357", {"start": v(36.2, -6.9) * mm, "end": v(36.72, -6.9) * mm});
            skLineSegment(sketch, "E358", {"start": v(36.72, -6.9) * mm, "end": v(36.9, -6.55) * mm});
            skLineSegment(sketch, "E359", {"start": v(36.9, -6.55) * mm, "end": v(37.14, -6.54) * mm});
            skLineSegment(sketch, "E360", {"start": v(37.14, -6.54) * mm, "end": v(37.3, -6.15) * mm});
            skLineSegment(sketch, "E361", {"start": v(37.3, -6.15) * mm, "end": v(37.5, -6.16) * mm});
            skLineSegment(sketch, "E362", {"start": v(37.5, -6.16) * mm, "end": v(37.67, -5.58) * mm});
            skLineSegment(sketch, "E363", {"start": v(37.67, -5.58) * mm, "end": v(37.9, -5.46) * mm});
            skLineSegment(sketch, "E364", {"start": v(37.9, -5.46) * mm, "end": v(38.02, -5.02) * mm});
            skLineSegment(sketch, "E365", {"start": v(38.02, -5.02) * mm, "end": v(38.27, -4.88) * mm});
            skLineSegment(sketch, "E366", {"start": v(38.27, -4.88) * mm, "end": v(38.27, -4.19) * mm});
            skLineSegment(sketch, "E367", {"start": v(38.27, -4.19) * mm, "end": v(38.64, -3.94) * mm});
            skLineSegment(sketch, "E368", {"start": v(38.64, -3.94) * mm, "end": v(38.65, -1.72) * mm});
            skLineSegment(sketch, "E369", {"start": v(38.65, -1.72) * mm, "end": v(39.1, -1.16) * mm});
            skLineSegment(sketch, "E370", {"start": v(39.1, -1.16) * mm, "end": v(39.1, 4.62) * mm});
            skLineSegment(sketch, "E371", {"start": v(39.1, 4.62) * mm, "end": v(39.02, 5.61) * mm});
            skLineSegment(sketch, "E372", {"start": v(39.02, 5.61) * mm, "end": v(38.7, 5.59) * mm});
            skLineSegment(sketch, "E373", {"start": v(38.7, 5.59) * mm, "end": v(38.7, 13.34) * mm});
            skLineSegment(sketch, "E374", {"start": v(38.7, 13.34) * mm, "end": v(38.33, 13.52) * mm});
            skLineSegment(sketch, "E375", {"start": v(38.33, 13.52) * mm, "end": v(38.3, 13.98) * mm});
            skLineSegment(sketch, "E376", {"start": v(38.3, 13.98) * mm, "end": v(37.9, 13.98) * mm});
            skLineSegment(sketch, "E377", {"start": v(37.9, 13.98) * mm, "end": v(37.9, 14.16) * mm});
            skLineSegment(sketch, "E378", {"start": v(37.9, 14.16) * mm, "end": v(37.57, 14.15) * mm});
            skLineSegment(sketch, "E379", {"start": v(37.57, 14.15) * mm, "end": v(37.57, 14.38) * mm});
            skLineSegment(sketch, "E380", {"start": v(37.57, 14.38) * mm, "end": v(37.08, 14.38) * mm});
            skLineSegment(sketch, "E381", {"start": v(37.08, 14.38) * mm, "end": v(37.07, 14.2) * mm});
            skLineSegment(sketch, "E382", {"start": v(37.07, 14.2) * mm, "end": v(36.73, 14.18) * mm});
            skLineSegment(sketch, "E383", {"start": v(36.73, 14.18) * mm, "end": v(36.7, 14.09) * mm});
            skLineSegment(sketch, "E384", {"start": v(36.7, 14.09) * mm, "end": v(36.31, 14.1) * mm});
            skLineSegment(sketch, "E385", {"start": v(36.31, 14.1) * mm, "end": v(36.3, 13.8) * mm});
            skLineSegment(sketch, "E386", {"start": v(36.3, 13.8) * mm, "end": v(35.98, 13.77) * mm});
            skLineSegment(sketch, "E387", {"start": v(35.98, 13.77) * mm, "end": v(35.77, 13.4) * mm});
            skLineSegment(sketch, "E388", {"start": v(35.77, 13.4) * mm, "end": v(35.76, 12.28) * mm});
            skLineSegment(sketch, "E389", {"start": v(35.76, 12.28) * mm, "end": v(35.83, 9.52) * mm});
            skLineSegment(sketch, "E390", {"start": v(35.83, 9.52) * mm, "end": v(35.81, 5.03) * mm});
            skLineSegment(sketch, "E391", {"start": v(35.81, 5.03) * mm, "end": v(35.78, -2.78) * mm});
            skLineSegment(sketch, "E392", {"start": v(35.78, -2.78) * mm, "end": v(35.93, -3.2) * mm});
            skLineSegment(sketch, "E393", {"start": v(35.93, -3.2) * mm, "end": v(35.66, -3.2) * mm});
            skLineSegment(sketch, "E394", {"start": v(35.66, -3.2) * mm, "end": v(35.52, -4.19) * mm});
            skLineSegment(sketch, "E395", {"start": v(35.52, -4.19) * mm, "end": v(35.24, -4.15) * mm});
            skLineSegment(sketch, "E396", {"start": v(35.24, -4.15) * mm, "end": v(35.2, -4.55) * mm});
            skLineSegment(sketch, "E397", {"start": v(35.2, -4.55) * mm, "end": v(34.82, -4.6) * mm});
            skLineSegment(sketch, "E398", {"start": v(34.82, -4.6) * mm, "end": v(34.79, -4.88) * mm});
            skLineSegment(sketch, "E399", {"start": v(34.79, -4.88) * mm, "end": v(34.4, -4.88) * mm});
            skLineSegment(sketch, "E400", {"start": v(34.4, -4.88) * mm, "end": v(34.3, -5.09) * mm});
            skLineSegment(sketch, "E401", {"start": v(34.3, -5.09) * mm, "end": v(34.27, -5.22) * mm});
            skLineSegment(sketch, "E402", {"start": v(34.27, -5.22) * mm, "end": v(33.93, -5.3) * mm});
            skLineSegment(sketch, "E403", {"start": v(33.93, -5.3) * mm, "end": v(33.39, -5.34) * mm});
            skLineSegment(sketch, "E404", {"start": v(33.39, -5.34) * mm, "end": v(33.04, -5.6) * mm});
            skLineSegment(sketch, "E405", {"start": v(33.04, -5.6) * mm, "end": v(32.53, -5.64) * mm});
            skLineSegment(sketch, "E406", {"start": v(32.53, -5.64) * mm, "end": v(32.31, -5.4) * mm});
            skLineSegment(sketch, "E407", {"start": v(32.31, -5.4) * mm, "end": v(32.1, -5.38) * mm});
            skLineSegment(sketch, "E408", {"start": v(32.1, -5.38) * mm, "end": v(31.85, -5.32) * mm});
            skLineSegment(sketch, "E409", {"start": v(31.85, -5.32) * mm, "end": v(31.48, -5.3) * mm});
            skLineSegment(sketch, "E410", {"start": v(31.48, -5.3) * mm, "end": v(31.45, -4.99) * mm});
            skLineSegment(sketch, "E411", {"start": v(31.45, -4.99) * mm, "end": v(31.06, -4.93) * mm});
            skLineSegment(sketch, "E412", {"start": v(31.06, -4.93) * mm, "end": v(30.66, -4.5) * mm});
            skLineSegment(sketch, "E413", {"start": v(30.66, -4.5) * mm, "end": v(30.38, -3.86) * mm});
            skLineSegment(sketch, "E414", {"start": v(30.38, -3.86) * mm, "end": v(29.93, -3.74) * mm});
            skLineSegment(sketch, "E415", {"start": v(29.93, -3.74) * mm, "end": v(29.85, -2.8) * mm});
            skLineSegment(sketch, "E416", {"start": v(29.85, -2.8) * mm, "end": v(29.63, -2.46) * mm});
            skLineSegment(sketch, "E417", {"start": v(29.63, -2.46) * mm, "end": v(29.58, 0) * mm});
            skLineSegment(sketch, "E418", {"start": v(29.58, 0) * mm, "end": v(29.58, 1.24) * mm});
            skLineSegment(sketch, "E419", {"start": v(29.58, 1.24) * mm, "end": v(29.64, 2.4) * mm});
            skLineSegment(sketch, "E420", {"start": v(29.64, 2.4) * mm, "end": v(29.64, 9.66) * mm});
            skLineSegment(sketch, "E421", {"start": v(29.64, 9.66) * mm, "end": v(29.64, 13.52) * mm});
            skLineSegment(sketch, "E422", {"start": v(29.64, 13.52) * mm, "end": v(29.6, 13.97) * mm});
            skLineSegment(sketch, "E423", {"start": v(29.6, 13.97) * mm, "end": v(29.28, 14.02) * mm});
            skLineSegment(sketch, "E424", {"start": v(29.28, 14.02) * mm, "end": v(29.22, 14.38) * mm});
            skLineSegment(sketch, "E425", {"start": v(29.22, 14.38) * mm, "end": v(29.1, 14.76) * mm});
            skLineSegment(sketch, "E426", {"start": v(-17.82, -9.88) * mm, "end": v(-18.38, -9.85) * mm});
            skLineSegment(sketch, "E427", {"start": v(-18.38, -9.85) * mm, "end": v(-18.38, -10.16) * mm});
            skLineSegment(sketch, "E428", {"start": v(-18.38, -10.16) * mm, "end": v(-18.67, -10.18) * mm});
            skLineSegment(sketch, "E429", {"start": v(-18.67, -10.18) * mm, "end": v(-18.75, -10.55) * mm});
            skLineSegment(sketch, "E430", {"start": v(-18.75, -10.55) * mm, "end": v(-19.06, -10.57) * mm});
            skLineSegment(sketch, "E431", {"start": v(-19.06, -10.57) * mm, "end": v(-19.23, -11.19) * mm});
            skLineSegment(sketch, "E432", {"start": v(-19.23, -11.19) * mm, "end": v(-19.43, -11.31) * mm});
            skLineSegment(sketch, "E433", {"start": v(-19.43, -11.31) * mm, "end": v(-19.52, -13.12) * mm});
            skLineSegment(sketch, "E434", {"start": v(-19.52, -13.12) * mm, "end": v(-19.8, -13.32) * mm});
            skLineSegment(sketch, "E435", {"start": v(-19.8, -13.32) * mm, "end": v(-19.8, -16.5) * mm});
            skLineSegment(sketch, "E436", {"start": v(-19.8, -16.5) * mm, "end": v(-19.52, -16.67) * mm});
            skLineSegment(sketch, "E437", {"start": v(-19.52, -16.67) * mm, "end": v(-19.46, -18.88) * mm});
            skLineSegment(sketch, "E438", {"start": v(-19.46, -18.88) * mm, "end": v(-19.13, -19.07) * mm});
            skLineSegment(sketch, "E439", {"start": v(-19.13, -19.07) * mm, "end": v(-19.07, -19.8) * mm});
            skLineSegment(sketch, "E440", {"start": v(-19.07, -19.8) * mm, "end": v(-18.8, -19.9) * mm});
            skLineSegment(sketch, "E441", {"start": v(-18.8, -19.9) * mm, "end": v(-18.77, -20.3) * mm});
            skLineSegment(sketch, "E442", {"start": v(-18.77, -20.3) * mm, "end": v(-18.66, -20.65) * mm});
            skLineSegment(sketch, "E443", {"start": v(-18.66, -20.65) * mm, "end": v(-18.32, -20.75) * mm});
            skLineSegment(sketch, "E444", {"start": v(-18.32, -20.75) * mm, "end": v(-18.3, -21.3) * mm});
            skLineSegment(sketch, "E445", {"start": v(-18.3, -21.3) * mm, "end": v(-17.97, -21.39) * mm});
            skLineSegment(sketch, "E446", {"start": v(-17.97, -21.39) * mm, "end": v(-17.94, -21.68) * mm});
            skLineSegment(sketch, "E447", {"start": v(-17.94, -21.68) * mm, "end": v(-17.61, -21.71) * mm});
            skLineSegment(sketch, "E448", {"start": v(-17.61, -21.71) * mm, "end": v(-17.57, -22.07) * mm});
            skLineSegment(sketch, "E449", {"start": v(-17.57, -22.07) * mm, "end": v(-17.23, -22.16) * mm});
            skLineSegment(sketch, "E450", {"start": v(-17.23, -22.16) * mm, "end": v(-17.26, -22.43) * mm});
            skLineSegment(sketch, "E451", {"start": v(-17.26, -22.43) * mm, "end": v(-16.65, -22.52) * mm});
            skLineSegment(sketch, "E452", {"start": v(-16.65, -22.52) * mm, "end": v(-16.6, -22.86) * mm});
            skLineSegment(sketch, "E453", {"start": v(-16.6, -22.86) * mm, "end": v(-15.76, -22.91) * mm});
            skLineSegment(sketch, "E454", {"start": v(-15.76, -22.91) * mm, "end": v(-15.88, -28.28) * mm});
            skLineSegment(sketch, "E455", {"start": v(-15.88, -28.28) * mm, "end": v(-15.65, -32.22) * mm});
            skLineSegment(sketch, "E456", {"start": v(-15.65, -32.22) * mm, "end": v(-15.27, -32.88) * mm});
            skLineSegment(sketch, "E457", {"start": v(-15.27, -32.88) * mm, "end": v(-15.26, -33.38) * mm});
            skLineSegment(sketch, "E458", {"start": v(-15.26, -33.38) * mm, "end": v(-14.91, -33.52) * mm});
            skLineSegment(sketch, "E459", {"start": v(-14.91, -33.52) * mm, "end": v(-14.89, -33.83) * mm});
            skLineSegment(sketch, "E460", {"start": v(-14.89, -33.83) * mm, "end": v(-14.51, -33.94) * mm});
            skLineSegment(sketch, "E461", {"start": v(-14.51, -33.94) * mm, "end": v(-13.85, -33.95) * mm});
            skLineSegment(sketch, "E462", {"start": v(-13.85, -33.95) * mm, "end": v(-13.29, -33.9) * mm});
            skLineSegment(sketch, "E463", {"start": v(-13.29, -33.9) * mm, "end": v(-13.01, -33.61) * mm});
            skLineSegment(sketch, "E464", {"start": v(-13.01, -33.61) * mm, "end": v(-12.9, -33.23) * mm});
            skLineSegment(sketch, "E465", {"start": v(-12.9, -33.23) * mm, "end": v(-12.6, -33.12) * mm});
            skLineSegment(sketch, "E466", {"start": v(-12.6, -33.12) * mm, "end": v(-12.5, -29.15) * mm});
            skLineSegment(sketch, "E467", {"start": v(-12.5, -29.15) * mm, "end": v(-12.5, -23.26) * mm});
            skLineSegment(sketch, "E468", {"start": v(-12.5, -23.26) * mm, "end": v(-12.47, -22.9) * mm});
            skLineSegment(sketch, "E469", {"start": v(-12.47, -22.9) * mm, "end": v(-11.87, -22.85) * mm});
            skLineSegment(sketch, "E470", {"start": v(-11.87, -22.85) * mm, "end": v(-11.83, -22.57) * mm});
            skLineSegment(sketch, "E471", {"start": v(-11.83, -22.57) * mm, "end": v(-11.36, -22.47) * mm});
            skLineSegment(sketch, "E472", {"start": v(-11.36, -22.47) * mm, "end": v(-11.38, -22.22) * mm});
            skLineSegment(sketch, "E473", {"start": v(-11.38, -22.22) * mm, "end": v(-11.05, -22.18) * mm});
            skLineSegment(sketch, "E474", {"start": v(-11.05, -22.18) * mm, "end": v(-10.93, -22.06) * mm});
            skLineSegment(sketch, "E475", {"start": v(-10.93, -22.06) * mm, "end": v(-10.7, -22.07) * mm});
            skLineSegment(sketch, "E476", {"start": v(-10.7, -22.07) * mm, "end": v(-10.68, -21.71) * mm});
            skLineSegment(sketch, "E477", {"start": v(-10.68, -21.71) * mm, "end": v(-10.4, -21.73) * mm});
            skLineSegment(sketch, "E478", {"start": v(-10.4, -21.73) * mm, "end": v(-10.1, -21.18) * mm});
            skLineSegment(sketch, "E479", {"start": v(-10.1, -21.18) * mm, "end": v(-9.87, -20.97) * mm});
            skLineSegment(sketch, "E480", {"start": v(-9.87, -20.97) * mm, "end": v(-9.54, -20.6) * mm});
            skLineSegment(sketch, "E481", {"start": v(-9.54, -20.6) * mm, "end": v(-9.2, -20.2) * mm});
            skLineSegment(sketch, "E482", {"start": v(-9.2, -20.2) * mm, "end": v(-9.1, -19.65) * mm});
            skLineSegment(sketch, "E483", {"start": v(-9.1, -19.65) * mm, "end": v(-8.8, -19.4) * mm});
            skLineSegment(sketch, "E484", {"start": v(-8.8, -19.4) * mm, "end": v(-8.73, -18.75) * mm});
            skLineSegment(sketch, "E485", {"start": v(-8.73, -18.75) * mm, "end": v(-8.45, -18.5) * mm});
            skLineSegment(sketch, "E486", {"start": v(-8.45, -18.5) * mm, "end": v(-8.32, -17.18) * mm});
            skLineSegment(sketch, "E487", {"start": v(-8.32, -17.18) * mm, "end": v(-8.05, -16.76) * mm});
            skLineSegment(sketch, "E488", {"start": v(-8.05, -16.76) * mm, "end": v(-7.74, -12.08) * mm});
            skLineSegment(sketch, "E489", {"start": v(-7.74, -12.08) * mm, "end": v(-7.97, -11.96) * mm});
            skLineSegment(sketch, "E490", {"start": v(-7.97, -11.96) * mm, "end": v(-8, -11.02) * mm});
            skLineSegment(sketch, "E491", {"start": v(-8, -11.02) * mm, "end": v(-8.34, -10.92) * mm});
            skLineSegment(sketch, "E492", {"start": v(-8.34, -10.92) * mm, "end": v(-8.36, -10.64) * mm});
            skLineSegment(sketch, "E493", {"start": v(-8.36, -10.64) * mm, "end": v(-8.93, -10.55) * mm});
            skLineSegment(sketch, "E494", {"start": v(-8.93, -10.55) * mm, "end": v(-8.9, -10.3) * mm});
            skLineSegment(sketch, "E495", {"start": v(-8.9, -10.3) * mm, "end": v(-9.94, -10.28) * mm});
            skLineSegment(sketch, "E496", {"start": v(-9.94, -10.28) * mm, "end": v(-9.99, -10.45) * mm});
            skLineSegment(sketch, "E497", {"start": v(-9.99, -10.45) * mm, "end": v(-10.11, -10.52) * mm});
            skLineSegment(sketch, "E498", {"start": v(-10.11, -10.52) * mm, "end": v(-10.3, -10.57) * mm});
            skLineSegment(sketch, "E499", {"start": v(-10.3, -10.57) * mm, "end": v(-10.44, -10.77) * mm});
            skLineSegment(sketch, "E500", {"start": v(-10.44, -10.77) * mm, "end": v(-10.55, -10.9) * mm});
            skLineSegment(sketch, "E501", {"start": v(-10.55, -10.9) * mm, "end": v(-10.72, -10.93) * mm});
            skLineSegment(sketch, "E502", {"start": v(-10.72, -10.93) * mm, "end": v(-10.79, -12.57) * mm});
            skLineSegment(sketch, "E503", {"start": v(-10.79, -12.57) * mm, "end": v(-10.94, -13.01) * mm});
            skLineSegment(sketch, "E504", {"start": v(-10.94, -13.01) * mm, "end": v(-11.08, -13.2) * mm});
            skLineSegment(sketch, "E505", {"start": v(-11.08, -13.2) * mm, "end": v(-11.2, -16.57) * mm});
            skLineSegment(sketch, "E506", {"start": v(-11.2, -16.57) * mm, "end": v(-11.38, -16.78) * mm});
            skLineSegment(sketch, "E507", {"start": v(-11.38, -16.78) * mm, "end": v(-11.51, -17.66) * mm});
            skLineSegment(sketch, "E508", {"start": v(-11.51, -17.66) * mm, "end": v(-11.78, -18.07) * mm});
            skLineSegment(sketch, "E509", {"start": v(-11.78, -18.07) * mm, "end": v(-11.93, -18.75) * mm});
            skLineSegment(sketch, "E510", {"start": v(-11.93, -18.75) * mm, "end": v(-12.19, -18.89) * mm});
            skLineSegment(sketch, "E511", {"start": v(-12.19, -18.89) * mm, "end": v(-12.34, -19.36) * mm});
            skLineSegment(sketch, "E512", {"start": v(-12.34, -19.36) * mm, "end": v(-12.6, -19.35) * mm});
            skLineSegment(sketch, "E513", {"start": v(-12.6, -19.35) * mm, "end": v(-12.63, -19.65) * mm});
            skLineSegment(sketch, "E514", {"start": v(-12.63, -19.65) * mm, "end": v(-13.12, -19.73) * mm});
            skLineSegment(sketch, "E515", {"start": v(-13.12, -19.73) * mm, "end": v(-13.17, -20.06) * mm});
            skLineSegment(sketch, "E516", {"start": v(-13.17, -20.06) * mm, "end": v(-14.59, -20.1) * mm});
            skLineSegment(sketch, "E517", {"start": v(-14.59, -20.1) * mm, "end": v(-15.09, -19.83) * mm});
            skLineSegment(sketch, "E518", {"start": v(-15.09, -19.83) * mm, "end": v(-15.65, -19.72) * mm});
            skLineSegment(sketch, "E519", {"start": v(-15.65, -19.72) * mm, "end": v(-15.63, -19.44) * mm});
            skLineSegment(sketch, "E520", {"start": v(-15.63, -19.44) * mm, "end": v(-16, -19.36) * mm});
            skLineSegment(sketch, "E521", {"start": v(-16, -19.36) * mm, "end": v(-16, -19.03) * mm});
            skLineSegment(sketch, "E522", {"start": v(-16, -19.03) * mm, "end": v(-16.35, -18.93) * mm});
            skLineSegment(sketch, "E523", {"start": v(-16.35, -18.93) * mm, "end": v(-16.38, -18.07) * mm});
            skLineSegment(sketch, "E524", {"start": v(-16.38, -18.07) * mm, "end": v(-16.72, -17.87) * mm});
            skLineSegment(sketch, "E525", {"start": v(-16.72, -17.87) * mm, "end": v(-16.72, -13.96) * mm});
            skLineSegment(sketch, "E526", {"start": v(-16.72, -13.96) * mm, "end": v(-16.98, -13.57) * mm});
            skLineSegment(sketch, "E527", {"start": v(-16.98, -13.57) * mm, "end": v(-17.1, -10.94) * mm});
            skLineSegment(sketch, "E528", {"start": v(-17.1, -10.94) * mm, "end": v(-17.13, -10.68) * mm});
            skLineSegment(sketch, "E529", {"start": v(-17.13, -10.68) * mm, "end": v(-17.4, -10.64) * mm});
            skLineSegment(sketch, "E530", {"start": v(-17.4, -10.64) * mm, "end": v(-17.4, -10.24) * mm});
            skLineSegment(sketch, "E531", {"start": v(-17.4, -10.24) * mm, "end": v(-17.5, -10.07) * mm});
            skLineSegment(sketch, "E532", {"start": v(-17.5, -10.07) * mm, "end": v(-17.75, -10.02) * mm});
            skLineSegment(sketch, "E533", {"start": v(-17.75, -10.02) * mm, "end": v(-17.82, -9.88) * mm});
            skLineSegment(sketch, "E534", {"start": v(-2.72, -11.03) * mm, "end": v(-3.12, -11.33) * mm});
            skLineSegment(sketch, "E535", {"start": v(-3.12, -11.33) * mm, "end": v(-3.12, -12.98) * mm});
            skLineSegment(sketch, "E536", {"start": v(-3.12, -12.98) * mm, "end": v(-2.83, -13.13) * mm});
            skLineSegment(sketch, "E537", {"start": v(-2.83, -13.13) * mm, "end": v(-2.79, -14.5) * mm});
            skLineSegment(sketch, "E538", {"start": v(-2.79, -14.5) * mm, "end": v(-2.46, -14.57) * mm});
            skLineSegment(sketch, "E539", {"start": v(-2.46, -14.57) * mm, "end": v(-2.36, -15.76) * mm});
            skLineSegment(sketch, "E540", {"start": v(-2.36, -15.76) * mm, "end": v(-2.1, -15.76) * mm});
            skLineSegment(sketch, "E541", {"start": v(-2.1, -15.76) * mm, "end": v(-2.04, -16.44) * mm});
            skLineSegment(sketch, "E542", {"start": v(-2.04, -16.44) * mm, "end": v(-1.7, -16.58) * mm});
            skLineSegment(sketch, "E543", {"start": v(-1.7, -16.58) * mm, "end": v(-1.68, -17.3) * mm});
            skLineSegment(sketch, "E544", {"start": v(-1.68, -17.3) * mm, "end": v(-1.33, -17.34) * mm});
            skLineSegment(sketch, "E545", {"start": v(-1.33, -17.34) * mm, "end": v(-1.26, -17.96) * mm});
            skLineSegment(sketch, "E546", {"start": v(-1.26, -17.96) * mm, "end": v(-0.9, -18.05) * mm});
            skLineSegment(sketch, "E547", {"start": v(-0.9, -18.05) * mm, "end": v(-0.87, -18.99) * mm});
            skLineSegment(sketch, "E548", {"start": v(-0.87, -18.99) * mm, "end": v(-0.5, -19.1) * mm});
            skLineSegment(sketch, "E549", {"start": v(-0.5, -19.1) * mm, "end": v(-0.53, -19.75) * mm});
            skLineSegment(sketch, "E550", {"start": v(-0.53, -19.75) * mm, "end": v(-0.18, -20) * mm});
            skLineSegment(sketch, "E551", {"start": v(-0.18, -20) * mm, "end": v(-0.18, -20.54) * mm});
            skLineSegment(sketch, "E552", {"start": v(-0.18, -20.54) * mm, "end": v(0.18, -20.69) * mm});
            skLineSegment(sketch, "E553", {"start": v(0.18, -20.69) * mm, "end": v(0.25, -21.34) * mm});
            skLineSegment(sketch, "E554", {"start": v(0.25, -21.34) * mm, "end": v(0.53, -21.41) * mm});
            skLineSegment(sketch, "E555", {"start": v(0.53, -21.41) * mm, "end": v(0.57, -22.95) * mm});
            skLineSegment(sketch, "E556", {"start": v(0.57, -22.95) * mm, "end": v(0.35, -23.2) * mm});
            skLineSegment(sketch, "E557", {"start": v(0.35, -23.2) * mm, "end": v(0.28, -24.16) * mm});
            skLineSegment(sketch, "E558", {"start": v(0.28, -24.16) * mm, "end": v(-0.04, -24.12) * mm});
            skLineSegment(sketch, "E559", {"start": v(-0.04, -24.12) * mm, "end": v(-0.14, -25.25) * mm});
            skLineSegment(sketch, "E560", {"start": v(-0.14, -25.25) * mm, "end": v(-0.46, -25.25) * mm});
            skLineSegment(sketch, "E561", {"start": v(-0.46, -25.25) * mm, "end": v(-0.59, -26.34) * mm});
            skLineSegment(sketch, "E562", {"start": v(-0.59, -26.34) * mm, "end": v(-0.84, -26.4) * mm});
            skLineSegment(sketch, "E563", {"start": v(-0.84, -26.4) * mm, "end": v(-0.9, -27.4) * mm});
            skLineSegment(sketch, "E564", {"start": v(-0.9, -27.4) * mm, "end": v(-1.21, -27.52) * mm});
            skLineSegment(sketch, "E565", {"start": v(-1.21, -27.52) * mm, "end": v(-1.24, -28.54) * mm});
            skLineSegment(sketch, "E566", {"start": v(-1.24, -28.54) * mm, "end": v(-1.55, -28.57) * mm});
            skLineSegment(sketch, "E567", {"start": v(-1.55, -28.57) * mm, "end": v(-1.7, -29.53) * mm});
            skLineSegment(sketch, "E568", {"start": v(-1.7, -29.53) * mm, "end": v(-1.94, -29.7) * mm});
            skLineSegment(sketch, "E569", {"start": v(-1.94, -29.7) * mm, "end": v(-2.05, -30.62) * mm});
            skLineSegment(sketch, "E570", {"start": v(-2.05, -30.62) * mm, "end": v(-2.32, -30.68) * mm});
            skLineSegment(sketch, "E571", {"start": v(-2.32, -30.68) * mm, "end": v(-2.47, -31.32) * mm});
            skLineSegment(sketch, "E572", {"start": v(-2.47, -31.32) * mm, "end": v(-2.72, -31.56) * mm});
            skLineSegment(sketch, "E573", {"start": v(-2.72, -31.56) * mm, "end": v(-2.72, -32.34) * mm});
            skLineSegment(sketch, "E574", {"start": v(-2.72, -32.34) * mm, "end": v(-2.43, -32.4) * mm});
            skLineSegment(sketch, "E575", {"start": v(-2.43, -32.4) * mm, "end": v(-2.44, -32.65) * mm});
            skLineSegment(sketch, "E576", {"start": v(-2.44, -32.65) * mm, "end": v(-2.18, -32.77) * mm});
            skLineSegment(sketch, "E577", {"start": v(-2.18, -32.77) * mm, "end": v(-2.07, -33.07) * mm});
            skLineSegment(sketch, "E578", {"start": v(-2.07, -33.07) * mm, "end": v(-1.75, -33.14) * mm});
            skLineSegment(sketch, "E579", {"start": v(-1.75, -33.14) * mm, "end": v(-1.64, -33.47) * mm});
            skLineSegment(sketch, "E580", {"start": v(-1.64, -33.47) * mm, "end": v(-0.45, -33.5) * mm});
            skLineSegment(sketch, "E581", {"start": v(-0.45, -33.5) * mm, "end": v(-0.41, -33.2) * mm});
            skLineSegment(sketch, "E582", {"start": v(-0.41, -33.2) * mm, "end": v(-0.03, -33.1) * mm});
            skLineSegment(sketch, "E583", {"start": v(-0.03, -33.1) * mm, "end": v(0, -32.8) * mm});
            skLineSegment(sketch, "E584", {"start": v(0, -32.8) * mm, "end": v(0.3, -32.76) * mm});
            skLineSegment(sketch, "E585", {"start": v(0.3, -32.76) * mm, "end": v(0.39, -32.22) * mm});
            skLineSegment(sketch, "E586", {"start": v(0.39, -32.22) * mm, "end": v(0.69, -31.99) * mm});
            skLineSegment(sketch, "E587", {"start": v(0.69, -31.99) * mm, "end": v(0.76, -31.2) * mm});
            skLineSegment(sketch, "E588", {"start": v(0.76, -31.2) * mm, "end": v(1.13, -30.86) * mm});
            skLineSegment(sketch, "E589", {"start": v(1.13, -30.86) * mm, "end": v(1.14, -30.18) * mm});
            skLineSegment(sketch, "E590", {"start": v(1.14, -30.18) * mm, "end": v(1.45, -30.08) * mm});
            skLineSegment(sketch, "E591", {"start": v(1.45, -30.08) * mm, "end": v(1.52, -29.2) * mm});
            skLineSegment(sketch, "E592", {"start": v(1.52, -29.2) * mm, "end": v(1.8, -29.04) * mm});
            skLineSegment(sketch, "E593", {"start": v(1.8, -29.04) * mm, "end": v(1.92, -28.2) * mm});
            skLineSegment(sketch, "E594", {"start": v(1.92, -28.2) * mm, "end": v(2.2, -28.15) * mm});
            skLineSegment(sketch, "E595", {"start": v(2.2, -28.15) * mm, "end": v(2.26, -27.2) * mm});
            skLineSegment(sketch, "E596", {"start": v(2.26, -27.2) * mm, "end": v(2.56, -27.04) * mm});
            skLineSegment(sketch, "E597", {"start": v(2.56, -27.04) * mm, "end": v(2.6, -26.78) * mm});
            skLineSegment(sketch, "E598", {"start": v(2.6, -26.78) * mm, "end": v(2.81, -26.67) * mm});
            skLineSegment(sketch, "E599", {"start": v(2.81, -26.67) * mm, "end": v(3.06, -26.65) * mm});
            skLineSegment(sketch, "E600", {"start": v(3.06, -26.65) * mm, "end": v(3.27, -26.82) * mm});
            skLineSegment(sketch, "E601", {"start": v(3.27, -26.82) * mm, "end": v(3.3, -27.4) * mm});
            skLineSegment(sketch, "E602", {"start": v(3.3, -27.4) * mm, "end": v(3.65, -27.52) * mm});
            skLineSegment(sketch, "E603", {"start": v(3.65, -27.52) * mm, "end": v(3.7, -28.17) * mm});
            skLineSegment(sketch, "E604", {"start": v(3.7, -28.17) * mm, "end": v(4.04, -28.23) * mm});
            skLineSegment(sketch, "E605", {"start": v(4.04, -28.23) * mm, "end": v(4.08, -28.93) * mm});
            skLineSegment(sketch, "E606", {"start": v(4.08, -28.93) * mm, "end": v(4.36, -29) * mm});
            skLineSegment(sketch, "E607", {"start": v(4.36, -29) * mm, "end": v(4.43, -29.7) * mm});
            skLineSegment(sketch, "E608", {"start": v(4.43, -29.7) * mm, "end": v(4.79, -29.79) * mm});
            skLineSegment(sketch, "E609", {"start": v(4.79, -29.79) * mm, "end": v(4.78, -30.45) * mm});
            skLineSegment(sketch, "E610", {"start": v(4.78, -30.45) * mm, "end": v(5.2, -30.52) * mm});
            skLineSegment(sketch, "E611", {"start": v(5.2, -30.52) * mm, "end": v(5.22, -31.2) * mm});
            skLineSegment(sketch, "E612", {"start": v(5.22, -31.2) * mm, "end": v(5.53, -31.28) * mm});
            skLineSegment(sketch, "E613", {"start": v(5.53, -31.28) * mm, "end": v(5.6, -32) * mm});
            skLineSegment(sketch, "E614", {"start": v(5.6, -32) * mm, "end": v(5.87, -32.04) * mm});
            skLineSegment(sketch, "E615", {"start": v(5.87, -32.04) * mm, "end": v(5.9, -32.34) * mm});
            skLineSegment(sketch, "E616", {"start": v(5.9, -32.34) * mm, "end": v(6.2, -32.47) * mm});
            skLineSegment(sketch, "E617", {"start": v(6.2, -32.47) * mm, "end": v(6.25, -32.72) * mm});
            skLineSegment(sketch, "E618", {"start": v(6.25, -32.72) * mm, "end": v(6.66, -32.8) * mm});
            skLineSegment(sketch, "E619", {"start": v(6.66, -32.8) * mm, "end": v(6.65, -33.09) * mm});
            skLineSegment(sketch, "E620", {"start": v(6.65, -33.09) * mm, "end": v(7.6, -33.13) * mm});
            skLineSegment(sketch, "E621", {"start": v(7.6, -33.13) * mm, "end": v(7.92, -32.78) * mm});
            skLineSegment(sketch, "E622", {"start": v(7.92, -32.78) * mm, "end": v(8.3, -32.73) * mm});
            skLineSegment(sketch, "E623", {"start": v(8.3, -32.73) * mm, "end": v(8.65, -32.13) * mm});
            skLineSegment(sketch, "E624", {"start": v(8.65, -32.13) * mm, "end": v(8.67, -31.12) * mm});
            skLineSegment(sketch, "E625", {"start": v(8.67, -31.12) * mm, "end": v(8.32, -30.7) * mm});
            skLineSegment(sketch, "E626", {"start": v(8.32, -30.7) * mm, "end": v(8.3, -30.05) * mm});
            skLineSegment(sketch, "E627", {"start": v(8.3, -30.05) * mm, "end": v(7.96, -29.8) * mm});
            skLineSegment(sketch, "E628", {"start": v(7.96, -29.8) * mm, "end": v(7.97, -29.16) * mm});
            skLineSegment(sketch, "E629", {"start": v(7.97, -29.16) * mm, "end": v(7.55, -29.12) * mm});
            skLineSegment(sketch, "E630", {"start": v(7.55, -29.12) * mm, "end": v(7.54, -28.41) * mm});
            skLineSegment(sketch, "E631", {"start": v(7.54, -28.41) * mm, "end": v(7.16, -28.41) * mm});
            skLineSegment(sketch, "E632", {"start": v(7.16, -28.41) * mm, "end": v(7.2, -27.7) * mm});
            skLineSegment(sketch, "E633", {"start": v(7.2, -27.7) * mm, "end": v(6.81, -27.68) * mm});
            skLineSegment(sketch, "E634", {"start": v(6.81, -27.68) * mm, "end": v(6.7, -26.83) * mm});
            skLineSegment(sketch, "E635", {"start": v(6.7, -26.83) * mm, "end": v(6.38, -26.1) * mm});
            skLineSegment(sketch, "E636", {"start": v(6.38, -26.1) * mm, "end": v(6.03, -25.38) * mm});
            skLineSegment(sketch, "E637", {"start": v(6.03, -25.38) * mm, "end": v(5.6, -24.7) * mm});
            skLineSegment(sketch, "E638", {"start": v(5.6, -24.7) * mm, "end": v(5.27, -23.8) * mm});
            skLineSegment(sketch, "E639", {"start": v(5.27, -23.8) * mm, "end": v(4.84, -23.13) * mm});
            skLineSegment(sketch, "E640", {"start": v(4.84, -23.13) * mm, "end": v(4.51, -22.37) * mm});
            skLineSegment(sketch, "E641", {"start": v(4.51, -22.37) * mm, "end": v(4.14, -22.06) * mm});
            skLineSegment(sketch, "E642", {"start": v(4.14, -22.06) * mm, "end": v(4.3, -21.08) * mm});
            skLineSegment(sketch, "E643", {"start": v(4.3, -21.08) * mm, "end": v(4.87, -19.9) * mm});
            skLineSegment(sketch, "E644", {"start": v(4.87, -19.9) * mm, "end": v(5.2, -18.7) * mm});
            skLineSegment(sketch, "E645", {"start": v(5.2, -18.7) * mm, "end": v(5.6, -17.4) * mm});
            skLineSegment(sketch, "E646", {"start": v(5.6, -17.4) * mm, "end": v(5.98, -16.12) * mm});
            skLineSegment(sketch, "E647", {"start": v(5.98, -16.12) * mm, "end": v(6.34, -15.2) * mm});
            skLineSegment(sketch, "E648", {"start": v(6.34, -15.2) * mm, "end": v(6.77, -13.74) * mm});
            skLineSegment(sketch, "E649", {"start": v(6.77, -13.74) * mm, "end": v(7.1, -12.26) * mm});
            skLineSegment(sketch, "E650", {"start": v(7.1, -12.26) * mm, "end": v(7.2, -11.18) * mm});
            skLineSegment(sketch, "E651", {"start": v(7.2, -11.18) * mm, "end": v(7.19, -10.64) * mm});
            skLineSegment(sketch, "E652", {"start": v(7.19, -10.64) * mm, "end": v(6.91, -10.48) * mm});
            skLineSegment(sketch, "E653", {"start": v(6.91, -10.48) * mm, "end": v(6.8, -10.28) * mm});
            skLineSegment(sketch, "E654", {"start": v(6.8, -10.28) * mm, "end": v(6.1, -10.27) * mm});
            skLineSegment(sketch, "E655", {"start": v(6.1, -10.27) * mm, "end": v(5.79, -10.48) * mm});
            skLineSegment(sketch, "E656", {"start": v(5.79, -10.48) * mm, "end": v(5.57, -10.58) * mm});
            skLineSegment(sketch, "E657", {"start": v(5.57, -10.58) * mm, "end": v(5.46, -10.82) * mm});
            skLineSegment(sketch, "E658", {"start": v(5.46, -10.82) * mm, "end": v(5.22, -10.95) * mm});
            skLineSegment(sketch, "E659", {"start": v(5.22, -10.95) * mm, "end": v(5.07, -11.26) * mm});
            skLineSegment(sketch, "E660", {"start": v(5.07, -11.26) * mm, "end": v(4.83, -11.64) * mm});
            skLineSegment(sketch, "E661", {"start": v(4.83, -11.64) * mm, "end": v(4.7, -11.97) * mm});
            skLineSegment(sketch, "E662", {"start": v(4.7, -11.97) * mm, "end": v(4.5, -12.07) * mm});
            skLineSegment(sketch, "E663", {"start": v(4.5, -12.07) * mm, "end": v(4.4, -12.63) * mm});
            skLineSegment(sketch, "E664", {"start": v(4.4, -12.63) * mm, "end": v(4.1, -12.73) * mm});
            skLineSegment(sketch, "E665", {"start": v(4.1, -12.73) * mm, "end": v(3.92, -13.34) * mm});
            skLineSegment(sketch, "E666", {"start": v(3.92, -13.34) * mm, "end": v(3.71, -13.82) * mm});
            skLineSegment(sketch, "E667", {"start": v(3.71, -13.82) * mm, "end": v(3.36, -14.66) * mm});
            skLineSegment(sketch, "E668", {"start": v(3.36, -14.66) * mm, "end": v(3.18, -15.34) * mm});
            skLineSegment(sketch, "E669", {"start": v(3.18, -15.34) * mm, "end": v(2.96, -15.79) * mm});
            skLineSegment(sketch, "E670", {"start": v(2.96, -15.79) * mm, "end": v(2.77, -16.3) * mm});
            skLineSegment(sketch, "E671", {"start": v(2.77, -16.3) * mm, "end": v(2.57, -16.73) * mm});
            skLineSegment(sketch, "E672", {"start": v(2.57, -16.73) * mm, "end": v(2.46, -17.43) * mm});
            skLineSegment(sketch, "E673", {"start": v(2.46, -17.43) * mm, "end": v(2.25, -17.7) * mm});
            skLineSegment(sketch, "E674", {"start": v(2.25, -17.7) * mm, "end": v(2, -17.63) * mm});
            skLineSegment(sketch, "E675", {"start": v(2, -17.63) * mm, "end": v(1.86, -17.4) * mm});
            skLineSegment(sketch, "E676", {"start": v(1.86, -17.4) * mm, "end": v(1.8, -17.13) * mm});
            skLineSegment(sketch, "E677", {"start": v(1.8, -17.13) * mm, "end": v(1.52, -17.08) * mm});
            skLineSegment(sketch, "E678", {"start": v(1.52, -17.08) * mm, "end": v(1.45, -16.6) * mm});
            skLineSegment(sketch, "E679", {"start": v(1.45, -16.6) * mm, "end": v(1.1, -16.18) * mm});
            skLineSegment(sketch, "E680", {"start": v(1.1, -16.18) * mm, "end": v(1.1, -15.86) * mm});
            skLineSegment(sketch, "E681", {"start": v(1.1, -15.86) * mm, "end": v(0.8, -15.6) * mm});
            skLineSegment(sketch, "E682", {"start": v(0.8, -15.6) * mm, "end": v(0.7, -15.18) * mm});
            skLineSegment(sketch, "E683", {"start": v(0.7, -15.18) * mm, "end": v(0.42, -15.02) * mm});
            skLineSegment(sketch, "E684", {"start": v(0.42, -15.02) * mm, "end": v(0.33, -14.42) * mm});
            skLineSegment(sketch, "E685", {"start": v(0.33, -14.42) * mm, "end": v(0.01, -14.3) * mm});
            skLineSegment(sketch, "E686", {"start": v(0.01, -14.3) * mm, "end": v(-0.07, -13.73) * mm});
            skLineSegment(sketch, "E687", {"start": v(-0.07, -13.73) * mm, "end": v(-0.41, -13.6) * mm});
            skLineSegment(sketch, "E688", {"start": v(-0.41, -13.6) * mm, "end": v(-0.36, -13.25) * mm});
            skLineSegment(sketch, "E689", {"start": v(-0.36, -13.25) * mm, "end": v(-0.76, -13.2) * mm});
            skLineSegment(sketch, "E690", {"start": v(-0.76, -13.2) * mm, "end": v(-0.8, -12.84) * mm});
            skLineSegment(sketch, "E691", {"start": v(-0.8, -12.84) * mm, "end": v(-1.13, -12.79) * mm});
            skLineSegment(sketch, "E692", {"start": v(-1.13, -12.79) * mm, "end": v(-1.17, -12.48) * mm});
            skLineSegment(sketch, "E693", {"start": v(-1.17, -12.48) * mm, "end": v(-1.58, -12.43) * mm});
            skLineSegment(sketch, "E694", {"start": v(-1.58, -12.43) * mm, "end": v(-1.57, -12.18) * mm});
            skLineSegment(sketch, "E695", {"start": v(-1.57, -12.18) * mm, "end": v(-1.6, -11.86) * mm});
            skLineSegment(sketch, "E696", {"start": v(-1.6, -11.86) * mm, "end": v(-1.88, -11.83) * mm});
            skLineSegment(sketch, "E697", {"start": v(-1.88, -11.83) * mm, "end": v(-1.98, -11.65) * mm});
            skLineSegment(sketch, "E698", {"start": v(-1.98, -11.65) * mm, "end": v(-2.16, -11.58) * mm});
            skLineSegment(sketch, "E699", {"start": v(-2.16, -11.58) * mm, "end": v(-2.26, -11.38) * mm});
            skLineSegment(sketch, "E700", {"start": v(-2.26, -11.38) * mm, "end": v(-2.49, -11.29) * mm});
            skLineSegment(sketch, "E701", {"start": v(-2.49, -11.29) * mm, "end": v(-2.51, -11.12) * mm});
            skLineSegment(sketch, "E702", {"start": v(-2.51, -11.12) * mm, "end": v(-2.72, -11.03) * mm});
            skLineSegment(sketch, "E703", {"start": v(13.62, -13.63) * mm, "end": v(13.79, -13.56) * mm});
            skLineSegment(sketch, "E704", {"start": v(13.79, -13.56) * mm, "end": v(13.93, -13.55) * mm});
            skLineSegment(sketch, "E705", {"start": v(13.93, -13.55) * mm, "end": v(13.96, -13.37) * mm});
            skLineSegment(sketch, "E706", {"start": v(13.96, -13.37) * mm, "end": v(14.25, -13.35) * mm});
            skLineSegment(sketch, "E707", {"start": v(14.25, -13.35) * mm, "end": v(15.83, -13.32) * mm});
            skLineSegment(sketch, "E708", {"start": v(15.83, -13.32) * mm, "end": v(18.46, -13.22) * mm});
            skLineSegment(sketch, "E709", {"start": v(18.46, -13.22) * mm, "end": v(18.95, -13.19) * mm});
            skLineSegment(sketch, "E710", {"start": v(18.95, -13.19) * mm, "end": v(19.42, -13.16) * mm});
            skLineSegment(sketch, "E711", {"start": v(19.42, -13.16) * mm, "end": v(19.53, -13.11) * mm});
            skLineSegment(sketch, "E712", {"start": v(19.53, -13.11) * mm, "end": v(19.64, -13.01) * mm});
            skLineSegment(sketch, "E713", {"start": v(19.64, -13.01) * mm, "end": v(19.74, -12.96) * mm});
            skLineSegment(sketch, "E714", {"start": v(19.74, -12.96) * mm, "end": v(20.58, -12.95) * mm});
            skLineSegment(sketch, "E715", {"start": v(20.58, -12.95) * mm, "end": v(21.11, -12.95) * mm});
            skLineSegment(sketch, "E716", {"start": v(21.11, -12.95) * mm, "end": v(21.53, -12.95) * mm});
            skLineSegment(sketch, "E717", {"start": v(21.53, -12.95) * mm, "end": v(21.56, -13.28) * mm});
            skLineSegment(sketch, "E718", {"start": v(21.56, -13.28) * mm, "end": v(21.95, -13.27) * mm});
            skLineSegment(sketch, "E719", {"start": v(21.95, -13.27) * mm, "end": v(21.99, -14.45) * mm});
            skLineSegment(sketch, "E720", {"start": v(21.99, -14.45) * mm, "end": v(21.69, -14.61) * mm});
            skLineSegment(sketch, "E721", {"start": v(21.69, -14.61) * mm, "end": v(21.58, -14.85) * mm});
            skLineSegment(sketch, "E722", {"start": v(21.58, -14.85) * mm, "end": v(20.28, -14.88) * mm});
            skLineSegment(sketch, "E723", {"start": v(20.28, -14.88) * mm, "end": v(18.5, -14.88) * mm});
            skLineSegment(sketch, "E724", {"start": v(18.5, -14.88) * mm, "end": v(18.14, -14.81) * mm});
            skLineSegment(sketch, "E725", {"start": v(18.14, -14.81) * mm, "end": v(17.88, -14.7) * mm});
            skLineSegment(sketch, "E726", {"start": v(17.88, -14.7) * mm, "end": v(17.65, -14.67) * mm});
            skLineSegment(sketch, "E727", {"start": v(17.65, -14.67) * mm, "end": v(14.8, -14.54) * mm});
            skLineSegment(sketch, "E728", {"start": v(14.8, -14.54) * mm, "end": v(13.58, -14.52) * mm});
            skLineSegment(sketch, "E729", {"start": v(13.58, -14.52) * mm, "end": v(13.46, -14.4) * mm});
            skLineSegment(sketch, "E730", {"start": v(13.46, -14.4) * mm, "end": v(13.28, -14.22) * mm});
            skLineSegment(sketch, "E731", {"start": v(13.28, -14.22) * mm, "end": v(13.2, -14.11) * mm});
            skLineSegment(sketch, "E732", {"start": v(13.2, -14.11) * mm, "end": v(13.3, -13.92) * mm});
            skLineSegment(sketch, "E733", {"start": v(13.3, -13.92) * mm, "end": v(13.46, -13.81) * mm});
            skLineSegment(sketch, "E734", {"start": v(13.46, -13.81) * mm, "end": v(13.51, -13.68) * mm});
            skLineSegment(sketch, "E735", {"start": v(13.51, -13.68) * mm, "end": v(13.62, -13.63) * mm});
            skLineSegment(sketch, "E736", {"start": v(13.18, -22.83) * mm, "end": v(13.43, -22.7) * mm});
            skLineSegment(sketch, "E737", {"start": v(13.43, -22.7) * mm, "end": v(13.5, -22.52) * mm});
            skLineSegment(sketch, "E738", {"start": v(13.5, -22.52) * mm, "end": v(13.56, -22.44) * mm});
            skLineSegment(sketch, "E739", {"start": v(13.56, -22.44) * mm, "end": v(13.8, -22.4) * mm});
            skLineSegment(sketch, "E740", {"start": v(13.8, -22.4) * mm, "end": v(13.94, -22.28) * mm});
            skLineSegment(sketch, "E741", {"start": v(13.94, -22.28) * mm, "end": v(13.96, -22.14) * mm});
            skLineSegment(sketch, "E742", {"start": v(13.96, -22.14) * mm, "end": v(14.05, -22.08) * mm});
            skLineSegment(sketch, "E743", {"start": v(14.05, -22.08) * mm, "end": v(15.08, -22.05) * mm});
            skLineSegment(sketch, "E744", {"start": v(15.08, -22.05) * mm, "end": v(16.6, -22.01) * mm});
            skLineSegment(sketch, "E745", {"start": v(16.6, -22.01) * mm, "end": v(17.67, -21.95) * mm});
            skLineSegment(sketch, "E746", {"start": v(17.67, -21.95) * mm, "end": v(17.83, -21.86) * mm});
            skLineSegment(sketch, "E747", {"start": v(17.83, -21.86) * mm, "end": v(18.33, -21.9) * mm});
            skLineSegment(sketch, "E748", {"start": v(18.33, -21.9) * mm, "end": v(18.43, -21.98) * mm});
            skLineSegment(sketch, "E749", {"start": v(18.43, -21.98) * mm, "end": v(18.81, -21.94) * mm});
            skLineSegment(sketch, "E750", {"start": v(18.81, -21.94) * mm, "end": v(18.98, -21.77) * mm});
            skLineSegment(sketch, "E751", {"start": v(18.98, -21.77) * mm, "end": v(19.1, -21.67) * mm});
            skLineSegment(sketch, "E752", {"start": v(19.1, -21.67) * mm, "end": v(19.99, -21.65) * mm});
            skLineSegment(sketch, "E753", {"start": v(19.99, -21.65) * mm, "end": v(20.4, -21.65) * mm});
            skLineSegment(sketch, "E754", {"start": v(20.4, -21.65) * mm, "end": v(20.49, -21.81) * mm});
            skLineSegment(sketch, "E755", {"start": v(20.49, -21.81) * mm, "end": v(20.58, -22.01) * mm});
            skLineSegment(sketch, "E756", {"start": v(20.58, -22.01) * mm, "end": v(20.83, -22) * mm});
            skLineSegment(sketch, "E757", {"start": v(20.83, -22) * mm, "end": v(20.9, -22.32) * mm});
            skLineSegment(sketch, "E758", {"start": v(20.9, -22.32) * mm, "end": v(21.03, -22.46) * mm});
            skLineSegment(sketch, "E759", {"start": v(21.03, -22.46) * mm, "end": v(21.15, -22.74) * mm});
            skLineSegment(sketch, "E760", {"start": v(21.15, -22.74) * mm, "end": v(21.1, -23.04) * mm});
            skLineSegment(sketch, "E761", {"start": v(21.1, -23.04) * mm, "end": v(20.92, -23.27) * mm});
            skLineSegment(sketch, "E762", {"start": v(20.92, -23.27) * mm, "end": v(20.63, -23.33) * mm});
            skLineSegment(sketch, "E763", {"start": v(20.63, -23.33) * mm, "end": v(20.48, -23.58) * mm});
            skLineSegment(sketch, "E764", {"start": v(20.48, -23.58) * mm, "end": v(20.02, -23.68) * mm});
            skLineSegment(sketch, "E765", {"start": v(20.02, -23.68) * mm, "end": v(19.27, -23.67) * mm});
            skLineSegment(sketch, "E766", {"start": v(19.27, -23.67) * mm, "end": v(17.98, -23.62) * mm});
            skLineSegment(sketch, "E767", {"start": v(17.98, -23.62) * mm, "end": v(17.72, -23.38) * mm});
            skLineSegment(sketch, "E768", {"start": v(17.72, -23.38) * mm, "end": v(17.32, -23.3) * mm});
            skLineSegment(sketch, "E769", {"start": v(17.32, -23.3) * mm, "end": v(16.48, -23.3) * mm});
            skLineSegment(sketch, "E770", {"start": v(16.48, -23.3) * mm, "end": v(15.3, -23.23) * mm});
            skLineSegment(sketch, "E771", {"start": v(15.3, -23.23) * mm, "end": v(14.3, -23.26) * mm});
            skLineSegment(sketch, "E772", {"start": v(14.3, -23.26) * mm, "end": v(13.6, -23.25) * mm});
            skLineSegment(sketch, "E773", {"start": v(13.6, -23.25) * mm, "end": v(13.53, -23.1) * mm});
            skLineSegment(sketch, "E774", {"start": v(13.53, -23.1) * mm, "end": v(13.49, -22.92) * mm});
            skLineSegment(sketch, "E775", {"start": v(13.49, -22.92) * mm, "end": v(13.35, -22.86) * mm});
            skLineSegment(sketch, "E776", {"start": v(13.35, -22.86) * mm, "end": v(13.24, -22.89) * mm});
            skLineSegment(sketch, "E777", {"start": v(13.24, -22.89) * mm, "end": v(13.18, -22.83) * mm});
            skLineSegment(sketch, "E778", {"start": v(13.18, -31.2) * mm, "end": v(13.53, -30.79) * mm});
            skLineSegment(sketch, "E779", {"start": v(13.53, -30.79) * mm, "end": v(14.24, -30.65) * mm});
            skLineSegment(sketch, "E780", {"start": v(14.24, -30.65) * mm, "end": v(15.14, -30.45) * mm});
            skLineSegment(sketch, "E781", {"start": v(15.14, -30.45) * mm, "end": v(18.35, -30.34) * mm});
            skLineSegment(sketch, "E782", {"start": v(18.35, -30.34) * mm, "end": v(18.95, -30.04) * mm});
            skLineSegment(sketch, "E783", {"start": v(18.95, -30.04) * mm, "end": v(19.6, -29.91) * mm});
            skLineSegment(sketch, "E784", {"start": v(19.6, -29.91) * mm, "end": v(20.1, -29.76) * mm});
            skLineSegment(sketch, "E785", {"start": v(20.1, -29.76) * mm, "end": v(20.66, -29.96) * mm});
            skLineSegment(sketch, "E786", {"start": v(20.66, -29.96) * mm, "end": v(20.96, -30.09) * mm});
            skLineSegment(sketch, "E787", {"start": v(20.96, -30.09) * mm, "end": v(20.96, -30.36) * mm});
            skLineSegment(sketch, "E788", {"start": v(20.96, -30.36) * mm, "end": v(21.26, -30.34) * mm});
            skLineSegment(sketch, "E789", {"start": v(21.26, -30.34) * mm, "end": v(21.33, -30.67) * mm});
            skLineSegment(sketch, "E790", {"start": v(21.33, -30.67) * mm, "end": v(21.48, -31) * mm});
            skLineSegment(sketch, "E791", {"start": v(21.48, -31) * mm, "end": v(21.53, -31.37) * mm});
            skLineSegment(sketch, "E792", {"start": v(21.53, -31.37) * mm, "end": v(21.4, -31.74) * mm});
            skLineSegment(sketch, "E793", {"start": v(21.4, -31.74) * mm, "end": v(21.03, -32.02) * mm});
            skLineSegment(sketch, "E794", {"start": v(21.03, -32.02) * mm, "end": v(20.63, -32.34) * mm});
            skLineSegment(sketch, "E795", {"start": v(20.63, -32.34) * mm, "end": v(19.75, -32.34) * mm});
            skLineSegment(sketch, "E796", {"start": v(19.75, -32.34) * mm, "end": v(19, -32.02) * mm});
            skLineSegment(sketch, "E797", {"start": v(19, -32.02) * mm, "end": v(15.17, -32) * mm});
            skLineSegment(sketch, "E798", {"start": v(15.17, -32) * mm, "end": v(14.57, -31.72) * mm});
            skLineSegment(sketch, "E799", {"start": v(14.57, -31.72) * mm, "end": v(14.15, -31.7) * mm});
            skLineSegment(sketch, "E800", {"start": v(14.15, -31.7) * mm, "end": v(13.52, -31.7) * mm});
            skLineSegment(sketch, "E801", {"start": v(13.52, -31.7) * mm, "end": v(13.18, -31.2) * mm});
            skLineSegment(sketch, "E802", {"start": v(-32.18, 4.7) * mm, "end": v(-30.65, 4.7) * mm});
            skLineSegment(sketch, "E803", {"start": v(-30.65, 4.7) * mm, "end": v(-30.4, 4.85) * mm});
            skLineSegment(sketch, "E804", {"start": v(-30.4, 4.85) * mm, "end": v(-29.33, 5.21) * mm});
            skLineSegment(sketch, "E805", {"start": v(-29.33, 5.21) * mm, "end": v(-28.61, 5.37) * mm});
            skLineSegment(sketch, "E806", {"start": v(-28.61, 5.37) * mm, "end": v(-27.76, 5.96) * mm});
            skLineSegment(sketch, "E807", {"start": v(-27.76, 5.96) * mm, "end": v(-27.03, 6.38) * mm});
            skLineSegment(sketch, "E808", {"start": v(-27.03, 6.38) * mm, "end": v(-26.69, 6.77) * mm});
            skLineSegment(sketch, "E809", {"start": v(-26.69, 6.77) * mm, "end": v(-26.2, 7.18) * mm});
            skLineSegment(sketch, "E810", {"start": v(-26.2, 7.18) * mm, "end": v(-25.9, 7.58) * mm});
            skLineSegment(sketch, "E811", {"start": v(-25.9, 7.58) * mm, "end": v(-25.87, 8.48) * mm});
            skLineSegment(sketch, "E812", {"start": v(-25.87, 8.48) * mm, "end": v(-25.52, 8.78) * mm});
            skLineSegment(sketch, "E813", {"start": v(-25.52, 8.78) * mm, "end": v(-25.52, 10.75) * mm});
            skLineSegment(sketch, "E814", {"start": v(-25.52, 10.75) * mm, "end": v(-25.87, 10.95) * mm});
            skLineSegment(sketch, "E815", {"start": v(-25.87, 10.95) * mm, "end": v(-25.87, 11.52) * mm});
            skLineSegment(sketch, "E816", {"start": v(-25.87, 11.52) * mm, "end": v(-26.24, 11.61) * mm});
            skLineSegment(sketch, "E817", {"start": v(-26.24, 11.61) * mm, "end": v(-26.3, 11.99) * mm});
            skLineSegment(sketch, "E818", {"start": v(-26.3, 11.99) * mm, "end": v(-26.65, 12.04) * mm});
            skLineSegment(sketch, "E819", {"start": v(-26.65, 12.04) * mm, "end": v(-26.81, 12.35) * mm});
            skLineSegment(sketch, "E820", {"start": v(-26.81, 12.35) * mm, "end": v(-27.38, 12.45) * mm});
            skLineSegment(sketch, "E821", {"start": v(-27.38, 12.45) * mm, "end": v(-27.53, 12.91) * mm});
            skLineSegment(sketch, "E822", {"start": v(-27.53, 12.91) * mm, "end": v(-28.16, 12.79) * mm});
            skLineSegment(sketch, "E823", {"start": v(-28.16, 12.79) * mm, "end": v(-28.2, 13.2) * mm});
            skLineSegment(sketch, "E824", {"start": v(-28.2, 13.2) * mm, "end": v(-29.9, 13.23) * mm});
            skLineSegment(sketch, "E825", {"start": v(-29.9, 13.23) * mm, "end": v(-30.07, 13.54) * mm});
            skLineSegment(sketch, "E826", {"start": v(-30.07, 13.54) * mm, "end": v(-32.5, 13.48) * mm});
            skLineSegment(sketch, "E827", {"start": v(-32.5, 13.48) * mm, "end": v(-32.64, 10.52) * mm});
            skLineSegment(sketch, "E828", {"start": v(-32.64, 10.52) * mm, "end": v(-32.4, 10.47) * mm});
            skLineSegment(sketch, "E829", {"start": v(-32.4, 10.47) * mm, "end": v(-32.18, 4.7) * mm});
            skLineSegment(sketch, "E830", {"start": v(-31.8, -5.35) * mm, "end": v(-30.64, -5.35) * mm});
            skLineSegment(sketch, "E831", {"start": v(-30.64, -5.35) * mm, "end": v(-30.31, -5.73) * mm});
            skLineSegment(sketch, "E832", {"start": v(-30.31, -5.73) * mm, "end": v(-29.43, -5.73) * mm});
            skLineSegment(sketch, "E833", {"start": v(-29.43, -5.73) * mm, "end": v(-29.03, -5.73) * mm});
            skLineSegment(sketch, "E834", {"start": v(-29.03, -5.73) * mm, "end": v(-28.8, -5.42) * mm});
            skLineSegment(sketch, "E835", {"start": v(-28.8, -5.42) * mm, "end": v(-27.96, -5.34) * mm});
            skLineSegment(sketch, "E836", {"start": v(-27.96, -5.34) * mm, "end": v(-27.76, -4.97) * mm});
            skLineSegment(sketch, "E837", {"start": v(-27.76, -4.97) * mm, "end": v(-27.45, -4.98) * mm});
            skLineSegment(sketch, "E838", {"start": v(-27.45, -4.98) * mm, "end": v(-27.37, -4.64) * mm});
            skLineSegment(sketch, "E839", {"start": v(-27.37, -4.64) * mm, "end": v(-27.08, -4.65) * mm});
            skLineSegment(sketch, "E840", {"start": v(-27.08, -4.65) * mm, "end": v(-27.03, -4.27) * mm});
            skLineSegment(sketch, "E841", {"start": v(-27.03, -4.27) * mm, "end": v(-26.8, -4.28) * mm});
            skLineSegment(sketch, "E842", {"start": v(-26.8, -4.28) * mm, "end": v(-26.64, -3.9) * mm});
            skLineSegment(sketch, "E843", {"start": v(-26.64, -3.9) * mm, "end": v(-26.44, -3.9) * mm});
            skLineSegment(sketch, "E844", {"start": v(-26.44, -3.9) * mm, "end": v(-26.29, -3.07) * mm});
            skLineSegment(sketch, "E845", {"start": v(-26.29, -3.07) * mm, "end": v(-25.94, -3.01) * mm});
            skLineSegment(sketch, "E846", {"start": v(-25.94, -3.01) * mm, "end": v(-25.87, -2.31) * mm});
            skLineSegment(sketch, "E847", {"start": v(-25.87, -2.31) * mm, "end": v(-25.53, -2.3) * mm});
            skLineSegment(sketch, "E848", {"start": v(-25.53, -2.3) * mm, "end": v(-25.44, -1.83) * mm});
            skLineSegment(sketch, "E849", {"start": v(-25.44, -1.83) * mm, "end": v(-25.48, -1.05) * mm});
            skLineSegment(sketch, "E850", {"start": v(-25.48, -1.05) * mm, "end": v(-25.5, -0.33) * mm});
            skLineSegment(sketch, "E851", {"start": v(-25.5, -0.33) * mm, "end": v(-25.5, 0.45) * mm});
            skLineSegment(sketch, "E852", {"start": v(-25.5, 0.45) * mm, "end": v(-25.6, 0.8) * mm});
            skLineSegment(sketch, "E853", {"start": v(-25.6, 0.8) * mm, "end": v(-25.89, 0.98) * mm});
            skLineSegment(sketch, "E854", {"start": v(-25.89, 0.98) * mm, "end": v(-25.94, 1.35) * mm});
            skLineSegment(sketch, "E855", {"start": v(-25.94, 1.35) * mm, "end": v(-26.22, 1.48) * mm});
            skLineSegment(sketch, "E856", {"start": v(-26.22, 1.48) * mm, "end": v(-26.32, 1.73) * mm});
            skLineSegment(sketch, "E857", {"start": v(-26.32, 1.73) * mm, "end": v(-26.8, 1.82) * mm});
            skLineSegment(sketch, "E858", {"start": v(-26.8, 1.82) * mm, "end": v(-27.14, 2.2) * mm});
            skLineSegment(sketch, "E859", {"start": v(-27.14, 2.2) * mm, "end": v(-28.16, 2.24) * mm});
            skLineSegment(sketch, "E860", {"start": v(-28.16, 2.24) * mm, "end": v(-28.52, 2.6) * mm});
            skLineSegment(sketch, "E861", {"start": v(-28.52, 2.6) * mm, "end": v(-31.86, 2.55) * mm});
            skLineSegment(sketch, "E862", {"start": v(-31.86, 2.55) * mm, "end": v(-31.93, 2.4) * mm});
            skLineSegment(sketch, "E863", {"start": v(-31.93, 2.4) * mm, "end": v(-31.93, 0.29) * mm});
            skLineSegment(sketch, "E864", {"start": v(-31.93, 0.29) * mm, "end": v(-32.14, -0.86) * mm});
            skLineSegment(sketch, "E865", {"start": v(-32.14, -0.86) * mm, "end": v(-32.31, -1.68) * mm});
            skLineSegment(sketch, "E866", {"start": v(-32.31, -1.68) * mm, "end": v(-32.35, -3.12) * mm});
            skLineSegment(sketch, "E867", {"start": v(-32.35, -3.12) * mm, "end": v(-32.18, -4.32) * mm});
            skLineSegment(sketch, "E868", {"start": v(-32.18, -4.32) * mm, "end": v(-31.8, -5.35) * mm});
            skLineSegment(sketch, "E869", {"start": v(14.33, -3.83) * mm, "end": v(14.67, -4.17) * mm});
            skLineSegment(sketch, "E870", {"start": v(14.67, -4.17) * mm, "end": v(14.82, -4.55) * mm});
            skLineSegment(sketch, "E871", {"start": v(14.82, -4.55) * mm, "end": v(15.08, -4.6) * mm});
            skLineSegment(sketch, "E872", {"start": v(15.08, -4.6) * mm, "end": v(15.18, -4.94) * mm});
            skLineSegment(sketch, "E873", {"start": v(15.18, -4.94) * mm, "end": v(15.49, -4.97) * mm});
            skLineSegment(sketch, "E874", {"start": v(15.49, -4.97) * mm, "end": v(15.5, -5.25) * mm});
            skLineSegment(sketch, "E875", {"start": v(15.5, -5.25) * mm, "end": v(18.07, -5.28) * mm});
            skLineSegment(sketch, "E876", {"start": v(18.07, -5.28) * mm, "end": v(18.15, -4.98) * mm});
            skLineSegment(sketch, "E877", {"start": v(18.15, -4.98) * mm, "end": v(18.85, -4.97) * mm});
            skLineSegment(sketch, "E878", {"start": v(18.85, -4.97) * mm, "end": v(18.86, -4.6) * mm});
            skLineSegment(sketch, "E879", {"start": v(18.86, -4.6) * mm, "end": v(19.2, -4.56) * mm});
            skLineSegment(sketch, "E880", {"start": v(19.2, -4.56) * mm, "end": v(19.3, -4.17) * mm});
            skLineSegment(sketch, "E881", {"start": v(19.3, -4.17) * mm, "end": v(19.64, -4.19) * mm});
            skLineSegment(sketch, "E882", {"start": v(19.64, -4.19) * mm, "end": v(19.68, -3.46) * mm});
            skLineSegment(sketch, "E883", {"start": v(19.68, -3.46) * mm, "end": v(20.04, -3.38) * mm});
            skLineSegment(sketch, "E884", {"start": v(20.04, -3.38) * mm, "end": v(20.06, 3.16) * mm});
            skLineSegment(sketch, "E885", {"start": v(20.06, 3.16) * mm, "end": v(20.06, 10.65) * mm});
            skLineSegment(sketch, "E886", {"start": v(20.06, 10.65) * mm, "end": v(19.65, 10.93) * mm});
            skLineSegment(sketch, "E887", {"start": v(19.65, 10.93) * mm, "end": v(19.68, 11.98) * mm});
            skLineSegment(sketch, "E888", {"start": v(19.68, 11.98) * mm, "end": v(19.3, 12.13) * mm});
            skLineSegment(sketch, "E889", {"start": v(19.3, 12.13) * mm, "end": v(19.29, 12.67) * mm});
            skLineSegment(sketch, "E890", {"start": v(19.29, 12.67) * mm, "end": v(18.9, 12.88) * mm});
            skLineSegment(sketch, "E891", {"start": v(18.9, 12.88) * mm, "end": v(18.82, 13.11) * mm});
            skLineSegment(sketch, "E892", {"start": v(18.82, 13.11) * mm, "end": v(16, 13.22) * mm});
            skLineSegment(sketch, "E893", {"start": v(16, 13.22) * mm, "end": v(15.91, 12.88) * mm});
            skLineSegment(sketch, "E894", {"start": v(15.91, 12.88) * mm, "end": v(15.44, 12.5) * mm});
            skLineSegment(sketch, "E895", {"start": v(15.44, 12.5) * mm, "end": v(14.77, 12.42) * mm});
            skLineSegment(sketch, "E896", {"start": v(14.77, 12.42) * mm, "end": v(14.76, 11.88) * mm});
            skLineSegment(sketch, "E897", {"start": v(14.76, 11.88) * mm, "end": v(14.4, 11.69) * mm});
            skLineSegment(sketch, "E898", {"start": v(14.4, 11.69) * mm, "end": v(14.35, 10.9) * mm});
            skLineSegment(sketch, "E899", {"start": v(14.35, 10.9) * mm, "end": v(14.1, 10.75) * mm});
            skLineSegment(sketch, "E900", {"start": v(14.1, 10.75) * mm, "end": v(14, 9.23) * mm});
            skLineSegment(sketch, "E901", {"start": v(14, 9.23) * mm, "end": v(14.14, 1.02) * mm});
            skLineSegment(sketch, "E902", {"start": v(14.14, 1.02) * mm, "end": v(14.33, -3.83) * mm});
            skSolve(sketch);
        }
        {
            var Q0;
            Q0 = qSketchRegion(id + "F0", true);
            extrude(context, id + "F1", {"entities" : qUnion([Q0]), "domain" : OperationDomain.MODEL, "flatOperationType" : FlatOperationType.REMOVE, "depth" : 25 * mm, "offsetDistance" : 25 * mm});
        }
    });
